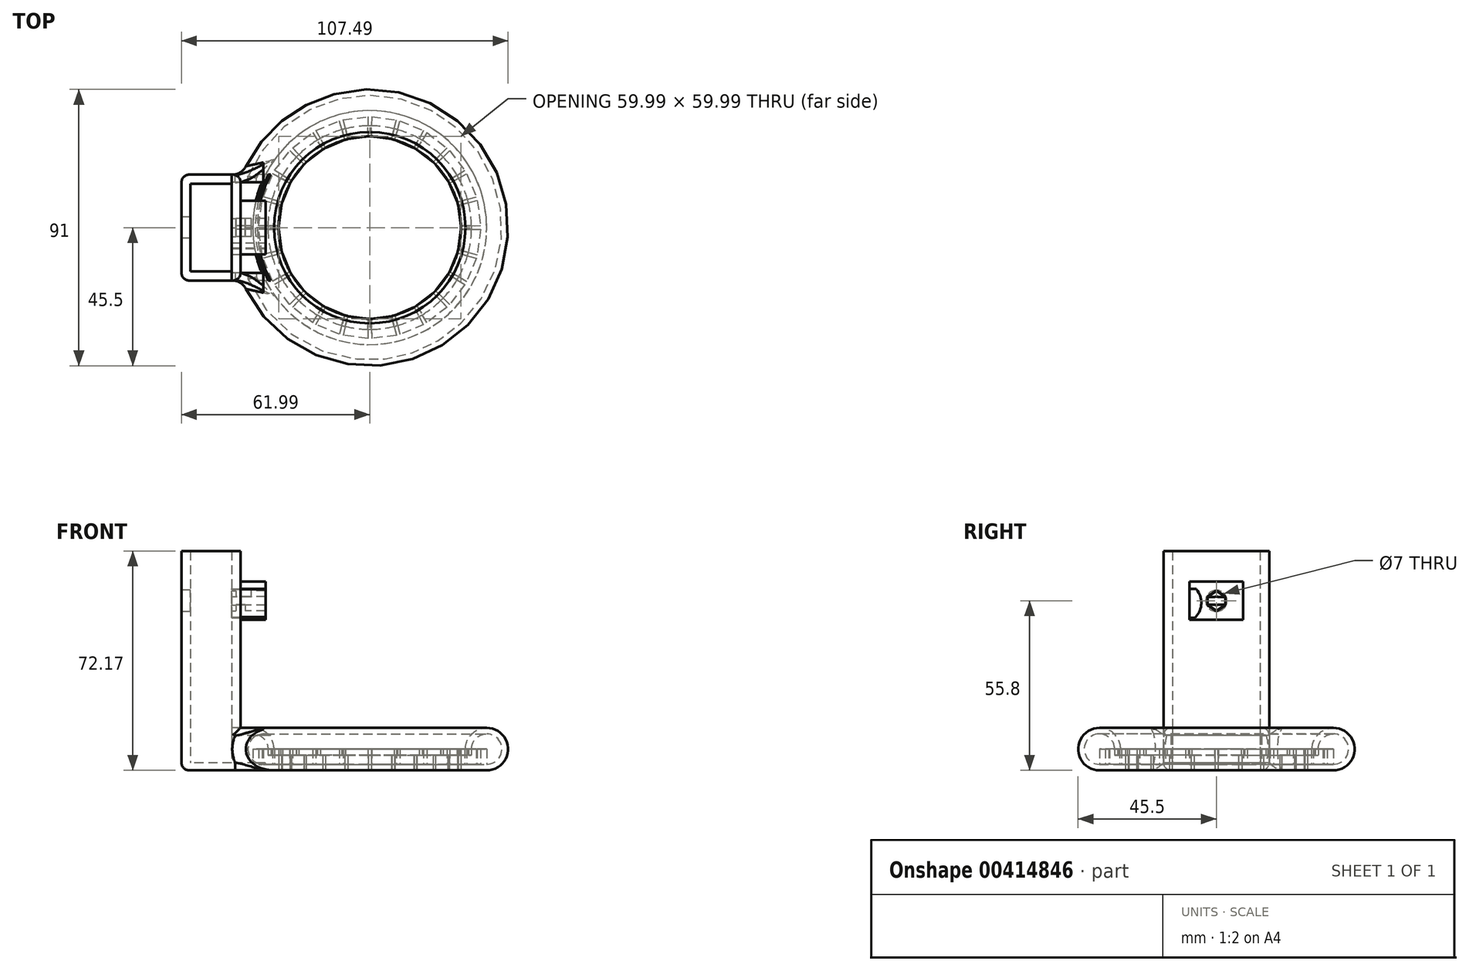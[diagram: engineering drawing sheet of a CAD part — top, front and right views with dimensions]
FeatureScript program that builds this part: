
annotation { "Feature Type Name" : "Feature", "Feature Type Description" : "" }
export const myFeature = defineFeature(function(context is Context, id is Id, definition is map)
    precondition{}
    {
        {
            var Q0;
            Q0=qCreatedBy(makeId("Right.planeOp"),FACE);
            cPlane(context, id + "F0", {"entities" : qUnion([Q0]), "cplaneType" : CPlaneType.OFFSET, "offset" : 42.5 * mm, "oppositeDirection" : true, "width" : 150 * mm, "height" : 150 * mm});
        }
        {
            var Q0;
            Q0=qCreatedBy(makeId("Front.planeOp"),FACE);
            cPlane(context, id + "F1", {"entities" : qUnion([Q0]), "cplaneType" : CPlaneType.OFFSET, "offset" : 17.41 * mm, "width" : 150 * mm, "height" : 150 * mm});
        }
        {
            var Q0;
            Q0=qCreatedBy(makeId("Front.planeOp"),FACE);
            cPlane(context, id + "F2", {"entities" : qUnion([Q0]), "cplaneType" : CPlaneType.OFFSET, "offset" : 17.41 * mm, "oppositeDirection" : true, "width" : 150 * mm, "height" : 150 * mm});
        }
        {
            var Q0;
            Q0=qCreatedBy(makeId("Top.planeOp"),FACE);
            cPlane(context, id + "F3", {"entities" : qUnion([Q0]), "cplaneType" : CPlaneType.OFFSET, "offset" : 7 * mm, "width" : 150 * mm, "height" : 150 * mm});
        }
        {
            var Q0;
            Q0=qCreatedBy(id+"F3.planeOp",FACE);
            cPlane(context, id + "F4", {"entities" : qUnion([Q0]), "cplaneType" : CPlaneType.OFFSET, "offset" : 6.95 * mm, "width" : 150 * mm, "height" : 150 * mm});
        }
        {
            var Q0;
            Q0=qCreatedBy(makeId("Right.planeOp"),FACE);
            cPlane(context, id + "F5", {"entities" : qUnion([Q0]), "cplaneType" : CPlaneType.OFFSET, "offset" : 62 * mm, "oppositeDirection" : true, "width" : 150 * mm, "height" : 150 * mm});
        }
        {
            var Q0;
            Q0=qCreatedBy(makeId("Top.planeOp"),FACE);
            var sketch = newSketch(context, id + "F6", { "sketchPlane" : qUnion([Q0])});
            skCircle(sketch, "E0", {"center": v(0, 0) * mm, "radius": 45 * mm});
            skCircle(sketch, "E1.0", {"center": v(0, 0) * mm, "radius": 38.5 * mm});
            skLineSegment(sketch, "E2", {"start": v(-136.41, 41.5) * mm, "end": v(-136.41, 35) * mm});
            skLineSegment(sketch, "E3", {"start": v(-128.72, 34) * mm, "end": v(-127.05, 40.28) * mm});
            skLineSegment(sketch, "E4", {"start": v(-118.16, 36.6) * mm, "end": v(-121.4, 30.99) * mm});
            skLineSegment(sketch, "E5", {"start": v(-115.15, 26.17) * mm, "end": v(-110.55, 30.76) * mm});
            skLineSegment(sketch, "E6", {"start": v(-110.44, 20.01) * mm, "end": v(-104.8, 23.26) * mm});
            skLineSegment(sketch, "E7", {"start": v(-107.45, 12.84) * mm, "end": v(-101.18, 14.54) * mm});
            skLineSegment(sketch, "E8", {"start": v(-106.41, 5.01) * mm, "end": v(-99.91, 5.01) * mm});
            skLineSegment(sketch, "E9.MirrorCS", {"start": v(-107.44, -2.81) * mm, "end": v(-101.17, -4.5) * mm});
            skLineSegment(sketch, "E10.MirrorCS", {"start": v(-110.42, -9.99) * mm, "end": v(-104.8, -13.24) * mm});
            skLineSegment(sketch, "E11.MirrorCS", {"start": v(-115.13, -16.15) * mm, "end": v(-110.52, -20.73) * mm});
            skLineSegment(sketch, "E12.MirrorCS", {"start": v(-118.13, -26.6) * mm, "end": v(-121.38, -20.97) * mm});
            skLineSegment(sketch, "E13.MirrorCS", {"start": v(-128.7, -24) * mm, "end": v(-127.02, -30.27) * mm});
            skLineSegment(sketch, "E14.MirrorCS", {"start": v(-144.1, 34) * mm, "end": v(-145.77, 40.28) * mm});
            skLineSegment(sketch, "E15.MirrorCS", {"start": v(-154.66, 36.6) * mm, "end": v(-151.41, 30.99) * mm});
            skLineSegment(sketch, "E16.MirrorCS", {"start": v(-157.67, 26.17) * mm, "end": v(-162.27, 30.76) * mm});
            skLineSegment(sketch, "E17.MirrorCS", {"start": v(-162.38, 20.01) * mm, "end": v(-168.01, 23.26) * mm});
            skLineSegment(sketch, "E18.MirrorCS", {"start": v(-165.37, 12.84) * mm, "end": v(-171.64, 14.54) * mm});
            skLineSegment(sketch, "E19.MirrorCS", {"start": v(-165.38, -2.81) * mm, "end": v(-171.65, -4.5) * mm});
            skLineSegment(sketch, "E20.MirrorCS", {"start": v(-162.4, -9.99) * mm, "end": v(-168.03, -13.24) * mm});
            skLineSegment(sketch, "E21.MirrorCS", {"start": v(-157.69, -16.15) * mm, "end": v(-162.3, -20.73) * mm});
            skLineSegment(sketch, "E22.MirrorCS", {"start": v(-154.69, -26.6) * mm, "end": v(-151.44, -20.97) * mm});
            skLineSegment(sketch, "E23.MirrorCS", {"start": v(-144.13, -24) * mm, "end": v(-145.8, -30.27) * mm});
            skLineSegment(sketch, "E24", {"start": v(-136.41, -25) * mm, "end": v(-136.41, -31.5) * mm});
            skLineSegment(sketch, "E25", {"start": v(-166.41, 5) * mm, "end": v(-172.91, 5) * mm});
            skCircle(sketch, "E26", {"center": v(-136.41, 5) * mm, "radius": 1.25 * mm, "construction": true});
            skLineSegment(sketch, "E27", {"start": v(0.64, 36.5) * mm, "end": v(0.52, 30) * mm});
            skLineSegment(sketch, "E28", {"start": v(8.2, 28.86) * mm, "end": v(9.97, 35.11) * mm});
            skLineSegment(sketch, "E29", {"start": v(18.8, 31.29) * mm, "end": v(15.46, 25.72) * mm});
            skLineSegment(sketch, "E30", {"start": v(21.62, 20.8) * mm, "end": v(26.3, 25.3) * mm});
            skLineSegment(sketch, "E31", {"start": v(26.23, 14.56) * mm, "end": v(31.92, 17.71) * mm});
            skLineSegment(sketch, "E32", {"start": v(29.1, 7.33) * mm, "end": v(35.4, 8.92) * mm});
            skLineSegment(sketch, "E33", {"start": v(30, -0.5) * mm, "end": v(36.5, -0.62) * mm});
            skLineSegment(sketch, "E34.MirrorCS", {"start": v(28.82, -8.32) * mm, "end": v(35.07, -10.12) * mm});
            skLineSegment(sketch, "E35.MirrorCS", {"start": v(25.72, -15.44) * mm, "end": v(31.3, -18.78) * mm});
            skLineSegment(sketch, "E36.MirrorCS", {"start": v(20.9, -21.52) * mm, "end": v(25.43, -26.18) * mm});
            skLineSegment(sketch, "E37.MirrorCS", {"start": v(17.73, -31.9) * mm, "end": v(14.57, -26.23) * mm});
            skLineSegment(sketch, "E38.MirrorCS", {"start": v(7.21, -29.12) * mm, "end": v(8.77, -35.43) * mm});
            skLineSegment(sketch, "E39.MirrorCS", {"start": v(-7.18, 29.13) * mm, "end": v(-8.74, 35.44) * mm});
            skLineSegment(sketch, "E40.MirrorCS", {"start": v(-17.7, 31.92) * mm, "end": v(-14.55, 26.25) * mm});
            skLineSegment(sketch, "E41.MirrorCS", {"start": v(-20.88, 21.54) * mm, "end": v(-25.4, 26.2) * mm});
            skLineSegment(sketch, "E42.MirrorCS", {"start": v(-25.7, 15.46) * mm, "end": v(-31.28, 18.81) * mm});
            skLineSegment(sketch, "E43.MirrorCS", {"start": v(-28.82, 8.34) * mm, "end": v(-35.06, 10.15) * mm});
            skLineSegment(sketch, "E44.MirrorCS", {"start": v(-29.1, -7.3) * mm, "end": v(-35.4, -8.89) * mm});
            skLineSegment(sketch, "E45.MirrorCS", {"start": v(-26.25, -14.53) * mm, "end": v(-31.93, -17.68) * mm});
            skLineSegment(sketch, "E46.MirrorCS", {"start": v(-21.64, -20.77) * mm, "end": v(-26.33, -25.28) * mm});
            skLineSegment(sketch, "E47.MirrorCS", {"start": v(-18.83, -31.27) * mm, "end": v(-15.48, -25.7) * mm});
            skLineSegment(sketch, "E48.MirrorCS", {"start": v(-8.22, -28.85) * mm, "end": v(-10, -35.1) * mm});
            skLineSegment(sketch, "E49", {"start": v(-0.52, -30) * mm, "end": v(-0.64, -36.5) * mm});
            skLineSegment(sketch, "E50", {"start": v(-30, 0.52) * mm, "end": v(-36.5, 0.64) * mm});
            skLineSegment(sketch, "E51", {"start": v(-0.64, 36.5) * mm, "end": v(-0.52, 30) * mm});
            skLineSegment(sketch, "E52", {"start": v(7.18, 29.13) * mm, "end": v(8.74, 35.44) * mm});
            skLineSegment(sketch, "E53", {"start": v(17.7, 31.92) * mm, "end": v(14.55, 26.25) * mm});
            skLineSegment(sketch, "E54", {"start": v(20.88, 21.54) * mm, "end": v(25.4, 26.2) * mm});
            skLineSegment(sketch, "E55", {"start": v(25.7, 15.46) * mm, "end": v(31.28, 18.81) * mm});
            skLineSegment(sketch, "E56", {"start": v(28.82, 8.34) * mm, "end": v(35.06, 10.15) * mm});
            skLineSegment(sketch, "E57", {"start": v(30, 0.54) * mm, "end": v(36.5, 0.65) * mm});
            skLineSegment(sketch, "E58.MirrorCS", {"start": v(29.1, -7.3) * mm, "end": v(35.4, -8.89) * mm});
            skLineSegment(sketch, "E59.MirrorCS", {"start": v(26.25, -14.53) * mm, "end": v(31.93, -17.68) * mm});
            skLineSegment(sketch, "E60.MirrorCS", {"start": v(21.64, -20.77) * mm, "end": v(26.33, -25.28) * mm});
            skLineSegment(sketch, "E61.MirrorCS", {"start": v(18.83, -31.27) * mm, "end": v(15.48, -25.7) * mm});
            skLineSegment(sketch, "E62.MirrorCS", {"start": v(8.22, -28.85) * mm, "end": v(10, -35.1) * mm});
            skLineSegment(sketch, "E63.MirrorCS", {"start": v(-8.2, 28.86) * mm, "end": v(-9.97, 35.11) * mm});
            skLineSegment(sketch, "E64.MirrorCS", {"start": v(-18.8, 31.29) * mm, "end": v(-15.46, 25.72) * mm});
            skLineSegment(sketch, "E65.MirrorCS", {"start": v(-21.62, 20.8) * mm, "end": v(-26.3, 25.3) * mm});
            skLineSegment(sketch, "E66.MirrorCS", {"start": v(-26.23, 14.56) * mm, "end": v(-31.92, 17.71) * mm});
            skLineSegment(sketch, "E67.MirrorCS", {"start": v(-29.1, 7.33) * mm, "end": v(-35.4, 8.92) * mm});
            skLineSegment(sketch, "E68.MirrorCS", {"start": v(-28.82, -8.32) * mm, "end": v(-35.07, -10.12) * mm});
            skLineSegment(sketch, "E69.MirrorCS", {"start": v(-25.72, -15.44) * mm, "end": v(-31.3, -18.78) * mm});
            skLineSegment(sketch, "E70.MirrorCS", {"start": v(-20.9, -21.52) * mm, "end": v(-25.43, -26.18) * mm});
            skLineSegment(sketch, "E71.MirrorCS", {"start": v(-17.73, -31.9) * mm, "end": v(-14.57, -26.23) * mm});
            skLineSegment(sketch, "E72.MirrorCS", {"start": v(-7.21, -29.12) * mm, "end": v(-8.77, -35.43) * mm});
            skLineSegment(sketch, "E73", {"start": v(0.52, -30) * mm, "end": v(0.64, -36.5) * mm});
            skLineSegment(sketch, "E74", {"start": v(-30, -0.52) * mm, "end": v(-36.5, -0.64) * mm});
            skCircle(sketch, "E75", {"center": v(0, 0) * mm, "radius": 1.25 * mm, "construction": true});
            skLineSegment(sketch, "E76", {"start": v(-29.1, 7.33) * mm, "end": v(-28.82, 8.34) * mm});
            skLineSegment(sketch, "E77", {"start": v(-28.82, 8.34) * mm, "end": v(-26.23, 14.56) * mm});
            skLineSegment(sketch, "E78", {"start": v(-26.23, 14.56) * mm, "end": v(-25.7, 15.46) * mm});
            skLineSegment(sketch, "E79", {"start": v(-25.7, 15.46) * mm, "end": v(-21.62, 20.8) * mm});
            skLineSegment(sketch, "E80", {"start": v(-21.62, 20.8) * mm, "end": v(-20.88, 21.54) * mm});
            skLineSegment(sketch, "E81", {"start": v(-20.88, 21.54) * mm, "end": v(-15.46, 25.72) * mm});
            skLineSegment(sketch, "E82", {"start": v(-15.46, 25.72) * mm, "end": v(-14.55, 26.25) * mm});
            skLineSegment(sketch, "E83", {"start": v(-14.55, 26.25) * mm, "end": v(-8.2, 28.86) * mm});
            skLineSegment(sketch, "E84", {"start": v(-8.2, 28.86) * mm, "end": v(-7.18, 29.13) * mm});
            skLineSegment(sketch, "E85", {"start": v(-7.18, 29.13) * mm, "end": v(-0.52, 30) * mm});
            skLineSegment(sketch, "E86", {"start": v(-0.52, 30) * mm, "end": v(0.52, 30) * mm});
            skLineSegment(sketch, "E87", {"start": v(0.52, 30) * mm, "end": v(7.18, 29.13) * mm});
            skLineSegment(sketch, "E88", {"start": v(7.18, 29.13) * mm, "end": v(8.2, 28.86) * mm});
            skLineSegment(sketch, "E89", {"start": v(8.2, 28.86) * mm, "end": v(14.55, 26.25) * mm});
            skLineSegment(sketch, "E90", {"start": v(14.55, 26.25) * mm, "end": v(15.46, 25.72) * mm});
            skLineSegment(sketch, "E91", {"start": v(15.46, 25.72) * mm, "end": v(20.88, 21.54) * mm});
            skLineSegment(sketch, "E92", {"start": v(20.88, 21.54) * mm, "end": v(21.62, 20.8) * mm});
            skLineSegment(sketch, "E93", {"start": v(21.62, 20.8) * mm, "end": v(25.7, 15.46) * mm});
            skLineSegment(sketch, "E94", {"start": v(25.7, 15.46) * mm, "end": v(26.23, 14.56) * mm});
            skLineSegment(sketch, "E95", {"start": v(26.23, 14.56) * mm, "end": v(28.82, 8.34) * mm});
            skLineSegment(sketch, "E96", {"start": v(28.82, 8.34) * mm, "end": v(29.1, 7.33) * mm});
            skLineSegment(sketch, "E97", {"start": v(29.1, 7.33) * mm, "end": v(30, 0.54) * mm});
            skLineSegment(sketch, "E98", {"start": v(30, 0.54) * mm, "end": v(30, -0.5) * mm});
            skLineSegment(sketch, "E99", {"start": v(30, -0.5) * mm, "end": v(29.1, -7.3) * mm});
            skLineSegment(sketch, "E100", {"start": v(29.1, -7.3) * mm, "end": v(28.82, -8.32) * mm});
            skLineSegment(sketch, "E101", {"start": v(28.82, -8.32) * mm, "end": v(26.25, -14.53) * mm});
            skLineSegment(sketch, "E102", {"start": v(26.25, -14.53) * mm, "end": v(25.72, -15.44) * mm});
            skLineSegment(sketch, "E103", {"start": v(25.72, -15.44) * mm, "end": v(21.64, -20.77) * mm});
            skLineSegment(sketch, "E104", {"start": v(21.64, -20.77) * mm, "end": v(20.9, -21.52) * mm});
            skLineSegment(sketch, "E105", {"start": v(20.9, -21.52) * mm, "end": v(15.48, -25.7) * mm});
            skLineSegment(sketch, "E106", {"start": v(15.48, -25.7) * mm, "end": v(14.57, -26.23) * mm});
            skLineSegment(sketch, "E107", {"start": v(14.57, -26.23) * mm, "end": v(8.22, -28.85) * mm});
            skLineSegment(sketch, "E108", {"start": v(8.22, -28.85) * mm, "end": v(7.21, -29.12) * mm});
            skLineSegment(sketch, "E109", {"start": v(7.21, -29.12) * mm, "end": v(0.52, -30) * mm});
            skLineSegment(sketch, "E110", {"start": v(0.52, -30) * mm, "end": v(-0.52, -30) * mm});
            skLineSegment(sketch, "E111", {"start": v(-0.52, -30) * mm, "end": v(-7.21, -29.12) * mm});
            skLineSegment(sketch, "E112", {"start": v(-7.21, -29.12) * mm, "end": v(-8.22, -28.85) * mm});
            skLineSegment(sketch, "E113", {"start": v(-8.22, -28.85) * mm, "end": v(-14.57, -26.23) * mm});
            skLineSegment(sketch, "E114", {"start": v(-14.57, -26.23) * mm, "end": v(-15.48, -25.7) * mm});
            skLineSegment(sketch, "E115", {"start": v(-15.48, -25.7) * mm, "end": v(-20.9, -21.52) * mm});
            skLineSegment(sketch, "E116", {"start": v(-20.9, -21.52) * mm, "end": v(-21.64, -20.77) * mm});
            skLineSegment(sketch, "E117", {"start": v(-21.64, -20.77) * mm, "end": v(-25.72, -15.44) * mm});
            skLineSegment(sketch, "E118", {"start": v(-25.72, -15.44) * mm, "end": v(-26.25, -14.53) * mm});
            skLineSegment(sketch, "E119", {"start": v(-28.82, -8.32) * mm, "end": v(-29.1, -7.3) * mm});
            skLineSegment(sketch, "E120", {"start": v(-26.25, -14.53) * mm, "end": v(-28.82, -8.32) * mm});
            skLineSegment(sketch, "E121", {"start": v(-29.1, -7.3) * mm, "end": v(-30, -0.52) * mm});
            skLineSegment(sketch, "E122", {"start": v(-30, -0.52) * mm, "end": v(-30, 0.52) * mm});
            skLineSegment(sketch, "E123", {"start": v(-30, 0.52) * mm, "end": v(-29.1, 7.33) * mm});
            skLineSegment(sketch, "E124", {"start": v(-36.5, 0.64) * mm, "end": v(-35.4, 8.92) * mm});
            skLineSegment(sketch, "E125", {"start": v(-35.06, 10.15) * mm, "end": v(-31.92, 17.71) * mm});
            skLineSegment(sketch, "E126", {"start": v(-31.28, 18.81) * mm, "end": v(-26.3, 25.3) * mm});
            skLineSegment(sketch, "E127", {"start": v(-25.4, 26.2) * mm, "end": v(-18.8, 31.29) * mm});
            skLineSegment(sketch, "E128", {"start": v(-17.7, 31.92) * mm, "end": v(-9.97, 35.11) * mm});
            skLineSegment(sketch, "E129", {"start": v(-8.74, 35.44) * mm, "end": v(-0.64, 36.5) * mm});
            skLineSegment(sketch, "E130", {"start": v(0.64, 36.5) * mm, "end": v(8.74, 35.44) * mm});
            skLineSegment(sketch, "E131", {"start": v(9.97, 35.11) * mm, "end": v(17.7, 31.92) * mm});
            skLineSegment(sketch, "E132", {"start": v(18.8, 31.29) * mm, "end": v(25.4, 26.2) * mm});
            skLineSegment(sketch, "E133", {"start": v(26.3, 25.3) * mm, "end": v(31.28, 18.81) * mm});
            skLineSegment(sketch, "E134", {"start": v(31.92, 17.71) * mm, "end": v(35.06, 10.15) * mm});
            skLineSegment(sketch, "E135", {"start": v(35.4, 8.92) * mm, "end": v(36.5, 0.65) * mm});
            skLineSegment(sketch, "E136", {"start": v(36.5, -0.62) * mm, "end": v(35.4, -8.89) * mm});
            skLineSegment(sketch, "E137", {"start": v(35.07, -10.12) * mm, "end": v(31.93, -17.68) * mm});
            skLineSegment(sketch, "E138", {"start": v(31.3, -18.78) * mm, "end": v(26.33, -25.28) * mm});
            skLineSegment(sketch, "E139", {"start": v(25.43, -26.18) * mm, "end": v(18.83, -31.27) * mm});
            skLineSegment(sketch, "E140", {"start": v(17.73, -31.9) * mm, "end": v(10, -35.1) * mm});
            skLineSegment(sketch, "E141", {"start": v(8.77, -35.43) * mm, "end": v(0.64, -36.5) * mm});
            skLineSegment(sketch, "E142", {"start": v(-0.64, -36.5) * mm, "end": v(-8.77, -35.43) * mm});
            skLineSegment(sketch, "E143", {"start": v(-10, -35.1) * mm, "end": v(-17.73, -31.9) * mm});
            skLineSegment(sketch, "E144", {"start": v(-18.83, -31.27) * mm, "end": v(-25.43, -26.18) * mm});
            skLineSegment(sketch, "E145", {"start": v(-26.33, -25.28) * mm, "end": v(-31.3, -18.78) * mm});
            skLineSegment(sketch, "E146", {"start": v(-31.93, -17.68) * mm, "end": v(-35.07, -10.12) * mm});
            skLineSegment(sketch, "E147", {"start": v(-35.4, -8.89) * mm, "end": v(-36.5, -0.64) * mm});
            skSolve(sketch);
        }
        {
            var Q0;
            Q0=qCreatedBy(makeId("Front.planeOp"),FACE);
            var sketch = newSketch(context, id + "F7", { "sketchPlane" : qUnion([Q0])});
            skLineSegment(sketch, "E148.bottom", {"start": v(38.5, 7) * mm, "end": v(-38.5, 7) * mm, "construction": true});
            skLineSegment(sketch, "E148.top", {"start": v(38.5, -7) * mm, "end": v(-38.5, -7) * mm, "construction": true});
            skLineSegment(sketch, "E148.left", {"start": v(38.5, 7) * mm, "end": v(38.5, -7) * mm, "construction": true});
            skLineSegment(sketch, "E148.right", {"start": v(-38.5, 7) * mm, "end": v(-38.5, -7) * mm, "construction": true});
            skPoint(sketch, "E148.middle", {"position": v(0, 0) * mm});
            skLineSegment(sketch, "E149", {"start": v(-38.5, 0) * mm, "end": v(38.5, 0) * mm, "construction": true});
            skArc(sketch, "E150", {"start": v(38.5, 0) * mm, "mid": v(43.45, 11.95) * mm, "end": v(31.5, 7) * mm});
            skArc(sketch, "E151", {"start": v(38.5, 2) * mm, "mid": v(42.04, 10.54) * mm, "end": v(33.5, 7) * mm});
            skLineSegment(sketch, "E152", {"start": v(38.5, 2) * mm, "end": v(38.5, 0) * mm});
            skLineSegment(sketch, "E153", {"start": v(38.5, 2) * mm, "end": v(31.5, 2) * mm, "construction": true});
            skLineSegment(sketch, "E154", {"start": v(31.5, 2) * mm, "end": v(31.5, 0) * mm, "construction": true});
            skLineSegment(sketch, "E155.0", {"start": v(38.5, 5) * mm, "end": v(-38.5, 5) * mm, "construction": true});
            skLineSegment(sketch, "E156", {"start": v(30, 0) * mm, "end": v(30, 7) * mm, "construction": true});
            skLineSegment(sketch, "E157", {"start": v(31.5, 7) * mm, "end": v(30, 7) * mm});
            skLineSegment(sketch, "E158", {"start": v(30, 7) * mm, "end": v(30, 5) * mm});
            skLineSegment(sketch, "E159", {"start": v(30, 5) * mm, "end": v(33.5, 5) * mm});
            skLineSegment(sketch, "E160", {"start": v(33.5, 5) * mm, "end": v(33.5, 7) * mm});
            skLineSegment(sketch, "E161", {"start": v(0, -7) * mm, "end": v(0, 7) * mm, "construction": true});
            skLineSegment(sketch, "E162", {"start": v(38.5, 7) * mm, "end": v(38.5, 14) * mm, "construction": true});
            skLineSegment(sketch, "E163", {"start": v(38.5, 7) * mm, "end": v(45.5, 7) * mm, "construction": true});
            skLineSegment(sketch, "E164", {"start": v(38.5, 12) * mm, "end": v(38.5, 14) * mm});
            skLineSegment(sketch, "E165", {"start": v(43.5, 7) * mm, "end": v(45.5, 7) * mm});
            skLineSegment(sketch, "E166.MirrorCS", {"start": v(-38.5, 2) * mm, "end": v(-38.5, 0) * mm});
            skLineSegment(sketch, "E167.MirrorCS", {"start": v(-30, 7) * mm, "end": v(-30, 5) * mm});
            skLineSegment(sketch, "E168.MirrorCS", {"start": v(-31.5, 7) * mm, "end": v(-30, 7) * mm});
            skLineSegment(sketch, "E169.MirrorCS", {"start": v(-33.5, 5) * mm, "end": v(-33.5, 7) * mm});
            skLineSegment(sketch, "E170.MirrorCS", {"start": v(-43.5, 7) * mm, "end": v(-45.5, 7) * mm});
            skLineSegment(sketch, "E171.MirrorCS", {"start": v(-30, 5) * mm, "end": v(-33.5, 5) * mm});
            skLineSegment(sketch, "E172.MirrorCS", {"start": v(-31.5, 2) * mm, "end": v(-31.5, 0) * mm, "construction": true});
            skLineSegment(sketch, "E173.MirrorCS", {"start": v(-38.5, 12) * mm, "end": v(-38.5, 14) * mm});
            skLineSegment(sketch, "E174.MirrorCS", {"start": v(-38.5, 7) * mm, "end": v(-45.5, 7) * mm, "construction": true});
            skLineSegment(sketch, "E175.MirrorCS", {"start": v(-38.5, 2) * mm, "end": v(-31.5, 2) * mm, "construction": true});
            skLineSegment(sketch, "E176.MirrorCS", {"start": v(-38.5, 7) * mm, "end": v(-38.5, 14) * mm, "construction": true});
            skArc(sketch, "E177.MirrorCS", {"start": v(-38.5, 0) * mm, "mid": v(-43.45, 11.95) * mm, "end": v(-31.5, 7) * mm});
            skArc(sketch, "E178.MirrorCS", {"start": v(-38.5, 2) * mm, "mid": v(-42.04, 10.54) * mm, "end": v(-33.5, 7) * mm});
            skLineSegment(sketch, "E179.MirrorCS", {"start": v(-38.5, 5) * mm, "end": v(38.5, 5) * mm, "construction": true});
            skLineSegment(sketch, "E180.MirrorCS", {"start": v(-30, 0) * mm, "end": v(-30, 7) * mm, "construction": true});
            skLineSegment(sketch, "E181.MirrorCS", {"start": v(-38.5, 7) * mm, "end": v(38.5, 7) * mm, "construction": true});
            skSolve(sketch);
        }
        {
            var Q0;
            Q0=qCreatedBy(id+"F0.planeOp",FACE);
            var sketch = newSketch(context, id + "F8", { "sketchPlane" : qUnion([Q0])});
            skLineSegment(sketch, "E182.bottom", {"start": v(45.5, 14) * mm, "end": v(-45.5, 14) * mm, "construction": true});
            skLineSegment(sketch, "E182.top", {"start": v(45.5, -14) * mm, "end": v(-45.5, -14) * mm, "construction": true});
            skLineSegment(sketch, "E182.left", {"start": v(45.5, 14) * mm, "end": v(45.5, -14) * mm, "construction": true});
            skLineSegment(sketch, "E182.right", {"start": v(-45.5, 14) * mm, "end": v(-45.5, -14) * mm, "construction": true});
            skPoint(sketch, "E182.middle", {"position": v(0, 0) * mm});
            skLineSegment(sketch, "E183", {"start": v(-45.5, 0) * mm, "end": v(45.5, 0) * mm, "construction": true});
            skLineSegment(sketch, "E184", {"start": v(0, 14) * mm, "end": v(0, -14) * mm, "construction": true});
            skLineSegment(sketch, "E185.0", {"start": v(-17.41, 14) * mm, "end": v(-17.41, -14) * mm, "construction": true});
            skLineSegment(sketch, "E186.MirrorCS", {"start": v(17.41, 14) * mm, "end": v(17.41, -14) * mm, "construction": true});
            skLineSegment(sketch, "E187.0", {"start": v(45.5, 7) * mm, "end": v(-45.5, 7) * mm, "construction": true});
            skLineSegment(sketch, "E188", {"start": v(-17.41, 14) * mm, "end": v(-17.41, 7) * mm});
            skLineSegment(sketch, "E189", {"start": v(-17.41, 7) * mm, "end": v(17.41, 7) * mm});
            skLineSegment(sketch, "E190", {"start": v(17.41, 7) * mm, "end": v(17.41, 14) * mm});
            skLineSegment(sketch, "E191", {"start": v(17.41, 14) * mm, "end": v(-17.41, 14) * mm});
            skLineSegment(sketch, "E192.0", {"start": v(45.5, 12) * mm, "end": v(-45.5, 12) * mm, "construction": true});
            skLineSegment(sketch, "E193.0", {"start": v(-14.73, 14) * mm, "end": v(-14.73, -14) * mm, "construction": true});
            skLineSegment(sketch, "E194.MirrorCS", {"start": v(14.73, 14) * mm, "end": v(14.73, -14) * mm, "construction": true});
            skLineSegment(sketch, "E195", {"start": v(-14.73, 7) * mm, "end": v(-14.73, 14) * mm});
            skLineSegment(sketch, "E196", {"start": v(14.73, 7) * mm, "end": v(14.73, 14) * mm});
            skLineSegment(sketch, "E197", {"start": v(17.41, 12) * mm, "end": v(-17.41, 12) * mm});
            skPoint(sketch, "E197.startSnap0", {"position": v(17.41, 10.5) * mm});
            skArc(sketch, "E198.0", {"start": v(6.63, 59.56) * mm, "mid": v(4.95, 54.97) * mm, "end": v(6.87, 50.47) * mm});
            skArc(sketch, "E199.MirrorCS", {"start": v(-6.63, 59.56) * mm, "mid": v(-4.95, 54.97) * mm, "end": v(-6.87, 50.47) * mm});
            skLineSegment(sketch, "E200", {"start": v(-6.63, 59.72) * mm, "end": v(6.63, 59.72) * mm});
            skLineSegment(sketch, "E201.1", {"start": v(-2.98, 51.95) * mm, "end": v(2.98, 51.95) * mm});
            skLineSegment(sketch, "E202", {"start": v(-8.8, 49.55) * mm, "end": v(-8.8, 62.12) * mm});
            skLineSegment(sketch, "E203.MirrorCS", {"start": v(8.8, 49.55) * mm, "end": v(8.8, 62.12) * mm});
            skLineSegment(sketch, "E204", {"start": v(-8.8, 62.12) * mm, "end": v(8.8, 62.12) * mm});
            skLineSegment(sketch, "E205", {"start": v(-6.63, 59.72) * mm, "end": v(-8.8, 59.72) * mm});
            skLineSegment(sketch, "E206", {"start": v(6.63, 59.72) * mm, "end": v(8.8, 59.72) * mm});
            skLineSegment(sketch, "E207", {"start": v(-2.98, 51.95) * mm, "end": v(-6.87, 50.26) * mm});
            skLineSegment(sketch, "E208", {"start": v(-6.87, 50.47) * mm, "end": v(-6.87, 50.26) * mm});
            skLineSegment(sketch, "E209.MirrorCS", {"start": v(2.98, 51.95) * mm, "end": v(6.87, 50.26) * mm});
            skLineSegment(sketch, "E210.MirrorCS", {"start": v(6.87, 50.47) * mm, "end": v(6.87, 50.26) * mm});
            skLineSegment(sketch, "E211", {"start": v(-8.8, 49.55) * mm, "end": v(8.8, 49.55) * mm});
            skLineSegment(sketch, "E212", {"start": v(6.87, 50.26) * mm, "end": v(8.8, 50.26) * mm});
            skLineSegment(sketch, "E213", {"start": v(-6.87, 50.26) * mm, "end": v(-8.8, 50.26) * mm});
            skCircle(sketch, "E214", {"center": v(0, 0) * mm, "radius": 1.5 * mm, "construction": true});
            skCircle(sketch, "E215", {"center": v(0, 55.8) * mm, "radius": 1.39 * mm});
            skLineSegment(sketch, "E216", {"start": v(6.63, 59.56) * mm, "end": v(6.63, 59.72) * mm});
            skLineSegment(sketch, "E217", {"start": v(-6.63, 59.56) * mm, "end": v(-6.63, 59.72) * mm});
            skLineSegment(sketch, "E218.1", {"start": v(0, 52.5) * mm, "end": v(2.95, 54.35) * mm});
            skLineSegment(sketch, "E218.2", {"start": v(-2.95, 54.35) * mm, "end": v(0, 52.5) * mm});
            skLineSegment(sketch, "E219.MirrorCS", {"start": v(0, 59.1) * mm, "end": v(2.95, 57.25) * mm});
            skLineSegment(sketch, "E220.MirrorCS", {"start": v(-2.95, 57.25) * mm, "end": v(0, 59.1) * mm});
            skLineSegment(sketch, "E221", {"start": v(2.95, 57.25) * mm, "end": v(2.95, 54.35) * mm});
            skLineSegment(sketch, "E222", {"start": v(-2.95, 57.25) * mm, "end": v(-2.95, 54.35) * mm});
            skCircle(sketch, "E223", {"center": v(0, 55.8) * mm, "radius": 1.25 * mm, "construction": true});
            skLineSegment(sketch, "E224", {"start": v(-2.95, 54.55) * mm, "end": v(2.95, 54.55) * mm});
            skLineSegment(sketch, "E225", {"start": v(-2.95, 57.05) * mm, "end": v(2.95, 57.05) * mm});
            skLineSegment(sketch, "E226", {"start": v(14.73, 14) * mm, "end": v(14.73, 52.5) * mm});
            skLineSegment(sketch, "E227", {"start": v(0, 55.8) * mm, "end": v(0, 14) * mm, "construction": true});
            skLineSegment(sketch, "E228.MirrorCS", {"start": v(-14.73, 14) * mm, "end": v(-14.73, 52.5) * mm});
            skLineSegment(sketch, "E229", {"start": v(17.41, 14) * mm, "end": v(17.41, 52.5) * mm});
            skLineSegment(sketch, "E230", {"start": v(-17.41, 14) * mm, "end": v(-17.41, 52.5) * mm});
            skLineSegment(sketch, "E231", {"start": v(17.41, 14) * mm, "end": v(17.41, 72.17) * mm});
            skLineSegment(sketch, "E232", {"start": v(17.41, 72.17) * mm, "end": v(-17.41, 72.17) * mm});
            skLineSegment(sketch, "E233", {"start": v(-17.41, 72.17) * mm, "end": v(-17.41, 52.5) * mm});
            skLineSegment(sketch, "E234", {"start": v(-14.73, 52.5) * mm, "end": v(-14.73, 72.17) * mm});
            skLineSegment(sketch, "E235", {"start": v(14.73, 52.5) * mm, "end": v(14.73, 72.17) * mm});
            skSolve(sketch);
        }
        {
            var Q0;
            Q0=qCreatedBy(id+"F1.planeOp",FACE);
            var sketch = newSketch(context, id + "F9", { "sketchPlane" : qUnion([Q0])});
            skLineSegment(sketch, "E236.bottom", {"start": v(45.5, 14) * mm, "end": v(-45.5, 14) * mm, "construction": true});
            skLineSegment(sketch, "E236.top", {"start": v(45.5, -14) * mm, "end": v(-45.5, -14) * mm, "construction": true});
            skLineSegment(sketch, "E236.left", {"start": v(45.5, 14) * mm, "end": v(45.5, -14) * mm, "construction": true});
            skLineSegment(sketch, "E236.right", {"start": v(-45.5, 14) * mm, "end": v(-45.5, -14) * mm, "construction": true});
            skPoint(sketch, "E236.middle", {"position": v(0, 0) * mm});
            skLineSegment(sketch, "E237", {"start": v(-45.5, 0) * mm, "end": v(45.5, 0) * mm, "construction": true});
            skLineSegment(sketch, "E238", {"start": v(0, 14) * mm, "end": v(0, -14) * mm, "construction": true});
            skLineSegment(sketch, "E239.0", {"start": v(-17.41, 14) * mm, "end": v(-17.41, -14) * mm, "construction": true});
            skLineSegment(sketch, "E240.MirrorCS", {"start": v(17.41, 14) * mm, "end": v(17.41, -14) * mm, "construction": true});
            skLineSegment(sketch, "E241.0", {"start": v(45.5, 7) * mm, "end": v(-45.5, 7) * mm, "construction": true});
            skLineSegment(sketch, "E242", {"start": v(-17.41, 14) * mm, "end": v(-17.41, 7) * mm});
            skLineSegment(sketch, "E243", {"start": v(-17.41, 7) * mm, "end": v(17.41, 7) * mm});
            skLineSegment(sketch, "E244", {"start": v(17.41, 7) * mm, "end": v(17.41, 14) * mm});
            skLineSegment(sketch, "E245", {"start": v(17.41, 14) * mm, "end": v(-17.41, 14) * mm});
            skLineSegment(sketch, "E246.0", {"start": v(45.5, 12) * mm, "end": v(-45.5, 12) * mm, "construction": true});
            skLineSegment(sketch, "E247.0", {"start": v(-14.73, 14) * mm, "end": v(-14.73, -14) * mm, "construction": true});
            skLineSegment(sketch, "E248.MirrorCS", {"start": v(14.73, 14) * mm, "end": v(14.73, -14) * mm, "construction": true});
            skLineSegment(sketch, "E249", {"start": v(-14.73, 7) * mm, "end": v(-14.73, 14) * mm});
            skLineSegment(sketch, "E250", {"start": v(14.73, 7) * mm, "end": v(14.73, 14) * mm});
            skLineSegment(sketch, "E251", {"start": v(17.41, 12) * mm, "end": v(-17.41, 12) * mm});
            skPoint(sketch, "E251.startSnap0", {"position": v(17.41, 10.5) * mm});
            skLineSegment(sketch, "E252", {"start": v(45.5, 14) * mm, "end": v(45.5, 7) * mm});
            skCircle(sketch, "E253", {"center": v(-35.07, 7) * mm, "radius": 7 * mm, "construction": true});
            skArc(sketch, "E254", {"start": v(-35.07, 12) * mm, "mid": v(-40.07, 7) * mm, "end": v(-35.07, 2) * mm});
            skLineSegment(sketch, "E255", {"start": v(-35.07, 12) * mm, "end": v(-35.07, 14) * mm});
            skLineSegment(sketch, "E256", {"start": v(-35.07, 14) * mm, "end": v(-45.5, 14) * mm});
            skLineSegment(sketch, "E257", {"start": v(-45.5, 14) * mm, "end": v(-45.5, 0) * mm});
            skLineSegment(sketch, "E258", {"start": v(-45.5, 0) * mm, "end": v(-35.07, 0) * mm});
            skLineSegment(sketch, "E259", {"start": v(-35.07, 0) * mm, "end": v(-35.07, 2) * mm});
            skLineSegment(sketch, "E260.MirrorCS", {"start": v(45.5, 2) * mm, "end": v(-45.5, 2) * mm, "construction": true});
            skCircle(sketch, "E261", {"center": v(0, 7) * mm, "radius": 1.25 * mm, "construction": true});
            skSolve(sketch);
        }
        {
            var Q0;
            Q0=qCreatedBy(id+"F2.planeOp",FACE);
            var sketch = newSketch(context, id + "F10", { "sketchPlane" : qUnion([Q0])});
            skLineSegment(sketch, "E262.bottom", {"start": v(45.5, 14) * mm, "end": v(-45.5, 14) * mm, "construction": true});
            skLineSegment(sketch, "E262.top", {"start": v(45.5, -14) * mm, "end": v(-45.5, -14) * mm, "construction": true});
            skLineSegment(sketch, "E262.left", {"start": v(45.5, 14) * mm, "end": v(45.5, -14) * mm, "construction": true});
            skLineSegment(sketch, "E262.right", {"start": v(-45.5, 14) * mm, "end": v(-45.5, -14) * mm, "construction": true});
            skPoint(sketch, "E262.middle", {"position": v(0, 0) * mm});
            skLineSegment(sketch, "E263", {"start": v(-45.5, 0) * mm, "end": v(45.5, 0) * mm, "construction": true});
            skLineSegment(sketch, "E264", {"start": v(0, 14) * mm, "end": v(0, -14) * mm, "construction": true});
            skLineSegment(sketch, "E265.0", {"start": v(-17.41, 14) * mm, "end": v(-17.41, -14) * mm, "construction": true});
            skLineSegment(sketch, "E266.MirrorCS", {"start": v(17.41, 14) * mm, "end": v(17.41, -14) * mm, "construction": true});
            skLineSegment(sketch, "E267.0", {"start": v(45.5, 7) * mm, "end": v(-45.5, 7) * mm, "construction": true});
            skLineSegment(sketch, "E268", {"start": v(-17.41, 14) * mm, "end": v(-17.41, 7) * mm});
            skLineSegment(sketch, "E269", {"start": v(-17.41, 7) * mm, "end": v(17.41, 7) * mm});
            skLineSegment(sketch, "E270", {"start": v(17.41, 7) * mm, "end": v(17.41, 14) * mm});
            skLineSegment(sketch, "E271", {"start": v(17.41, 14) * mm, "end": v(-17.41, 14) * mm});
            skLineSegment(sketch, "E272.0", {"start": v(45.5, 12) * mm, "end": v(-45.5, 12) * mm, "construction": true});
            skLineSegment(sketch, "E273.0", {"start": v(-14.73, 14) * mm, "end": v(-14.73, -14) * mm, "construction": true});
            skLineSegment(sketch, "E274.MirrorCS", {"start": v(14.73, 14) * mm, "end": v(14.73, -14) * mm, "construction": true});
            skLineSegment(sketch, "E275", {"start": v(-14.73, 7) * mm, "end": v(-14.73, 14) * mm});
            skLineSegment(sketch, "E276", {"start": v(14.73, 7) * mm, "end": v(14.73, 14) * mm});
            skLineSegment(sketch, "E277", {"start": v(17.41, 12) * mm, "end": v(-17.41, 12) * mm});
            skPoint(sketch, "E277.startSnap0", {"position": v(17.41, 10.5) * mm});
            skLineSegment(sketch, "E278", {"start": v(45.5, 14) * mm, "end": v(45.5, 7) * mm});
            skCircle(sketch, "E279", {"center": v(-35.07, 7) * mm, "radius": 7 * mm, "construction": true});
            skArc(sketch, "E280", {"start": v(-35.07, 12) * mm, "mid": v(-40.07, 7) * mm, "end": v(-35.07, 2) * mm});
            skLineSegment(sketch, "E281", {"start": v(-35.07, 12) * mm, "end": v(-35.07, 14) * mm});
            skLineSegment(sketch, "E282", {"start": v(-35.07, 14) * mm, "end": v(-45.5, 14) * mm});
            skLineSegment(sketch, "E283", {"start": v(-45.5, 14) * mm, "end": v(-45.5, 0) * mm});
            skLineSegment(sketch, "E284", {"start": v(-45.5, 0) * mm, "end": v(-35.07, 0) * mm});
            skLineSegment(sketch, "E285", {"start": v(-35.07, 0) * mm, "end": v(-35.07, 2) * mm});
            skLineSegment(sketch, "E286.MirrorCS", {"start": v(45.5, 2) * mm, "end": v(-45.5, 2) * mm, "construction": true});
            skCircle(sketch, "E287", {"center": v(0, 7) * mm, "radius": 1.25 * mm, "construction": true});
            skSolve(sketch);
        }
        {
            var Q0;
            Q0=qCreatedBy(makeId("Top.planeOp"),FACE);
            var sketch = newSketch(context, id + "F11", { "sketchPlane" : qUnion([Q0])});
            skPoint(sketch, "E288.middle", {"position": v(0, 0) * mm});
            skCircle(sketch, "E289", {"center": v(0, 0) * mm, "radius": 2.5 * mm, "construction": true});
            skLineSegment(sketch, "E290.MirrorCS", {"start": v(-32.65, 17.41) * mm, "end": v(-45.5, 17.41) * mm});
            skLineSegment(sketch, "E291.MirrorCS", {"start": v(-32.65, -17.41) * mm, "end": v(-45.5, -17.41) * mm});
            skLineSegment(sketch, "E292.MirrorCS", {"start": v(-45.5, 17.41) * mm, "end": v(-45.5, -17.41) * mm});
            skArc(sketch, "E293", {"start": v(-32.65, 17.41) * mm, "mid": v(-37, 0) * mm, "end": v(-32.65, -17.41) * mm});
            skLineSegment(sketch, "E294.bottom", {"start": v(-45.5, 8.28) * mm, "end": v(-45.5, -8.52) * mm, "construction": true});
            skLineSegment(sketch, "E294.left", {"start": v(-45.5, 8.28) * mm, "end": v(-59, 8.28) * mm, "construction": true});
            skLineSegment(sketch, "E295", {"start": v(-45.5, -8.52) * mm, "end": v(-59, -8.52) * mm, "construction": true});
            skLineSegment(sketch, "E296", {"start": v(-59, -8.52) * mm, "end": v(-59, 8.28) * mm, "construction": true});
            skLineSegment(sketch, "E297", {"start": v(-45.5, 8.28) * mm, "end": v(-59, -8.52) * mm, "construction": true});
            skLineSegment(sketch, "E298", {"start": v(-45.5, -8.52) * mm, "end": v(-59, 8.28) * mm, "construction": true});
            skLineSegment(sketch, "E299", {"start": v(-52.24, 0) * mm, "end": v(-42.5, 0) * mm, "construction": true});
            skLineSegment(sketch, "E300", {"start": v(-27.2, 0) * mm, "end": v(-42.4, 0) * mm, "construction": true});
            skLineSegment(sketch, "E301.0", {"start": v(-62, -8.52) * mm, "end": v(-62, 8.28) * mm, "construction": true});
            skLineSegment(sketch, "E302", {"start": v(-45.5, 17.41) * mm, "end": v(-62, 17.41) * mm});
            skLineSegment(sketch, "E303", {"start": v(-62, 17.41) * mm, "end": v(-62, -17.41) * mm});
            skLineSegment(sketch, "E304", {"start": v(-62, -17.41) * mm, "end": v(-45.5, -17.41) * mm});
            skLineSegment(sketch, "E305.0", {"start": v(-59, -14.41) * mm, "end": v(-45.5, -14.41) * mm});
            skLineSegment(sketch, "E305.1", {"start": v(-59, 14.41) * mm, "end": v(-59, -14.41) * mm});
            skLineSegment(sketch, "E305.2", {"start": v(-45.5, 14.41) * mm, "end": v(-59, 14.41) * mm});
            skSolve(sketch);
        }
        {
            var Q0;
            Q0=qCreatedBy(id+"F4.planeOp",FACE);
            var sketch = newSketch(context, id + "F12", { "sketchPlane" : qUnion([Q0])});
            skPoint(sketch, "E306.middle", {"position": v(0, 0) * mm});
            skCircle(sketch, "E307", {"center": v(0, 0) * mm, "radius": 2.5 * mm, "construction": true});
            skLineSegment(sketch, "E308.MirrorCS", {"start": v(-32.65, 17.41) * mm, "end": v(-45.5, 17.41) * mm});
            skLineSegment(sketch, "E309.MirrorCS", {"start": v(-32.65, -17.41) * mm, "end": v(-45.5, -17.41) * mm});
            skLineSegment(sketch, "E310.MirrorCS", {"start": v(-45.5, 17.41) * mm, "end": v(-45.5, -17.41) * mm});
            skArc(sketch, "E311", {"start": v(-32.65, 17.41) * mm, "mid": v(-37, 0) * mm, "end": v(-32.65, -17.41) * mm});
            skLineSegment(sketch, "E312.bottom", {"start": v(-45.5, 8.28) * mm, "end": v(-45.5, -8.52) * mm, "construction": true});
            skLineSegment(sketch, "E312.left", {"start": v(-45.5, 8.28) * mm, "end": v(-59, 8.28) * mm, "construction": true});
            skLineSegment(sketch, "E313", {"start": v(-45.5, -8.52) * mm, "end": v(-59, -8.52) * mm, "construction": true});
            skLineSegment(sketch, "E314", {"start": v(-59, -8.52) * mm, "end": v(-59, 8.28) * mm, "construction": true});
            skLineSegment(sketch, "E315", {"start": v(-45.5, 8.28) * mm, "end": v(-59, -8.52) * mm, "construction": true});
            skLineSegment(sketch, "E316", {"start": v(-45.5, -8.52) * mm, "end": v(-59, 8.28) * mm, "construction": true});
            skLineSegment(sketch, "E317", {"start": v(-52.24, 0) * mm, "end": v(-42.5, 0) * mm, "construction": true});
            skLineSegment(sketch, "E318", {"start": v(-27.2, 0) * mm, "end": v(-42.4, 0) * mm, "construction": true});
            skLineSegment(sketch, "E319.0", {"start": v(-62, -8.52) * mm, "end": v(-62, 8.28) * mm, "construction": true});
            skLineSegment(sketch, "E320", {"start": v(-45.5, 17.41) * mm, "end": v(-62, 17.41) * mm});
            skLineSegment(sketch, "E321", {"start": v(-62, 17.41) * mm, "end": v(-62, -17.41) * mm});
            skLineSegment(sketch, "E322", {"start": v(-62, -17.41) * mm, "end": v(-45.5, -17.41) * mm});
            skLineSegment(sketch, "E323.0", {"start": v(-59, -14.41) * mm, "end": v(-45.5, -14.41) * mm});
            skLineSegment(sketch, "E323.1", {"start": v(-59, 14.41) * mm, "end": v(-59, -14.41) * mm});
            skLineSegment(sketch, "E323.2", {"start": v(-45.5, 14.41) * mm, "end": v(-59, 14.41) * mm});
            skLineSegment(sketch, "E324.0", {"start": v(-42.5, 17.41) * mm, "end": v(-42.5, -17.41) * mm});
            skSolve(sketch);
        }
        {
            var Q0;
            Q0=makeQuery(id+"F6.imprint","IMPRINT",FACE,{"disambiguationData":[TD([[makeQuery(id+"F6.imprint","IMPRINT",EDGE,{"derivedFrom":sQuery(id+"F6.wireOp",EDGE,"E1.0")}),1.0]])]});
            extrude(context, id + "F13", {"entities" : qUnion([Q0]), "depth" : 7 * mm});
        }
        {
            var Q0;
            Q0=makeQuery(id+"F6.imprint","IMPRINT",FACE,{"disambiguationData":[TD([[makeQuery(id+"F6.imprint","IMPRINT",EDGE,{"derivedFrom":sQuery(id+"F6.wireOp",EDGE,"E50")}),-1.0]])]});
            var Q1;
            Q1=makeQuery(id+"F6.imprint","IMPRINT",FACE,{"disambiguationData":[TD([[makeQuery(id+"F6.imprint","IMPRINT",EDGE,{"derivedFrom":sQuery(id+"F6.wireOp",EDGE,"E43.MirrorCS")}),-1.0]])]});
            var Q2;
            Q2=makeQuery(id+"F6.imprint","IMPRINT",FACE,{"disambiguationData":[TD([[makeQuery(id+"F6.imprint","IMPRINT",EDGE,{"derivedFrom":sQuery(id+"F6.wireOp",EDGE,"E42.MirrorCS")}),-1.0]])]});
            var Q3;
            Q3=makeQuery(id+"F6.imprint","IMPRINT",FACE,{"disambiguationData":[TD([[makeQuery(id+"F6.imprint","IMPRINT",EDGE,{"derivedFrom":sQuery(id+"F6.wireOp",EDGE,"E41.MirrorCS")}),-1.0]])]});
            var Q4;
            Q4=makeQuery(id+"F6.imprint","IMPRINT",FACE,{"disambiguationData":[TD([[makeQuery(id+"F6.imprint","IMPRINT",EDGE,{"derivedFrom":sQuery(id+"F6.wireOp",EDGE,"E40.MirrorCS")}),1.0]])]});
            var Q5;
            Q5=makeQuery(id+"F6.imprint","IMPRINT",FACE,{"disambiguationData":[TD([[makeQuery(id+"F6.imprint","IMPRINT",EDGE,{"derivedFrom":sQuery(id+"F6.wireOp",EDGE,"E39.MirrorCS")}),-1.0]])]});
            var Q6;
            Q6=makeQuery(id+"F6.imprint","IMPRINT",FACE,{"disambiguationData":[TD([[makeQuery(id+"F6.imprint","IMPRINT",EDGE,{"derivedFrom":sQuery(id+"F6.wireOp",EDGE,"E27")}),1.0]])]});
            var Q7;
            Q7=makeQuery(id+"F6.imprint","IMPRINT",FACE,{"disambiguationData":[TD([[makeQuery(id+"F6.imprint","IMPRINT",EDGE,{"derivedFrom":sQuery(id+"F6.wireOp",EDGE,"E28")}),-1.0]])]});
            var Q8;
            Q8=makeQuery(id+"F6.imprint","IMPRINT",FACE,{"disambiguationData":[TD([[makeQuery(id+"F6.imprint","IMPRINT",EDGE,{"derivedFrom":sQuery(id+"F6.wireOp",EDGE,"E29")}),1.0]])]});
            var Q9;
            Q9=makeQuery(id+"F6.imprint","IMPRINT",FACE,{"disambiguationData":[TD([[makeQuery(id+"F6.imprint","IMPRINT",EDGE,{"derivedFrom":sQuery(id+"F6.wireOp",EDGE,"E30")}),-1.0]])]});
            var Q10;
            Q10=makeQuery(id+"F6.imprint","IMPRINT",FACE,{"disambiguationData":[TD([[makeQuery(id+"F6.imprint","IMPRINT",EDGE,{"derivedFrom":sQuery(id+"F6.wireOp",EDGE,"E31")}),-1.0]])]});
            var Q11;
            Q11=makeQuery(id+"F6.imprint","IMPRINT",FACE,{"disambiguationData":[TD([[makeQuery(id+"F6.imprint","IMPRINT",EDGE,{"derivedFrom":sQuery(id+"F6.wireOp",EDGE,"E32")}),-1.0]])]});
            var Q12;
            Q12=makeQuery(id+"F6.imprint","IMPRINT",FACE,{"disambiguationData":[TD([[makeQuery(id+"F6.imprint","IMPRINT",EDGE,{"derivedFrom":sQuery(id+"F6.wireOp",EDGE,"E33")}),-1.0]])]});
            var Q13;
            Q13=makeQuery(id+"F6.imprint","IMPRINT",FACE,{"disambiguationData":[TD([[makeQuery(id+"F6.imprint","IMPRINT",EDGE,{"derivedFrom":sQuery(id+"F6.wireOp",EDGE,"E34.MirrorCS")}),-1.0]])]});
            var Q14;
            Q14=makeQuery(id+"F6.imprint","IMPRINT",FACE,{"disambiguationData":[TD([[makeQuery(id+"F6.imprint","IMPRINT",EDGE,{"derivedFrom":sQuery(id+"F6.wireOp",EDGE,"E35.MirrorCS")}),-1.0]])]});
            var Q15;
            Q15=makeQuery(id+"F6.imprint","IMPRINT",FACE,{"disambiguationData":[TD([[makeQuery(id+"F6.imprint","IMPRINT",EDGE,{"derivedFrom":sQuery(id+"F6.wireOp",EDGE,"E36.MirrorCS")}),-1.0]])]});
            var Q16;
            Q16=makeQuery(id+"F6.imprint","IMPRINT",FACE,{"disambiguationData":[TD([[makeQuery(id+"F6.imprint","IMPRINT",EDGE,{"derivedFrom":sQuery(id+"F6.wireOp",EDGE,"E37.MirrorCS")}),1.0]])]});
            var Q17;
            Q17=makeQuery(id+"F6.imprint","IMPRINT",FACE,{"disambiguationData":[TD([[makeQuery(id+"F6.imprint","IMPRINT",EDGE,{"derivedFrom":sQuery(id+"F6.wireOp",EDGE,"E38.MirrorCS")}),-1.0]])]});
            var Q18;
            Q18=makeQuery(id+"F6.imprint","IMPRINT",FACE,{"disambiguationData":[TD([[makeQuery(id+"F6.imprint","IMPRINT",EDGE,{"derivedFrom":sQuery(id+"F6.wireOp",EDGE,"E49")}),-1.0]])]});
            var Q19;
            Q19=makeQuery(id+"F6.imprint","IMPRINT",FACE,{"disambiguationData":[TD([[makeQuery(id+"F6.imprint","IMPRINT",EDGE,{"derivedFrom":sQuery(id+"F6.wireOp",EDGE,"E48.MirrorCS")}),-1.0]])]});
            var Q20;
            Q20=makeQuery(id+"F6.imprint","IMPRINT",FACE,{"disambiguationData":[TD([[makeQuery(id+"F6.imprint","IMPRINT",EDGE,{"derivedFrom":sQuery(id+"F6.wireOp",EDGE,"E47.MirrorCS")}),1.0]])]});
            var Q21;
            Q21=makeQuery(id+"F6.imprint","IMPRINT",FACE,{"disambiguationData":[TD([[makeQuery(id+"F6.imprint","IMPRINT",EDGE,{"derivedFrom":sQuery(id+"F6.wireOp",EDGE,"E46.MirrorCS")}),-1.0]])]});
            var Q22;
            Q22=makeQuery(id+"F6.imprint","IMPRINT",FACE,{"disambiguationData":[TD([[makeQuery(id+"F6.imprint","IMPRINT",EDGE,{"derivedFrom":sQuery(id+"F6.wireOp",EDGE,"E45.MirrorCS")}),-1.0]])]});
            var Q23;
            Q23=makeQuery(id+"F6.imprint","IMPRINT",FACE,{"disambiguationData":[TD([[makeQuery(id+"F6.imprint","IMPRINT",EDGE,{"derivedFrom":sQuery(id+"F6.wireOp",EDGE,"E44.MirrorCS")}),-1.0]])]});
            extrude(context, id + "F14", {"entities" : qUnion([Q0, Q1, Q2, Q3, Q4, Q5, Q6, Q7, Q8, Q9, Q10, Q11, Q12, Q13, Q14, Q15, Q16, Q17, Q18, Q19, Q20, Q21, Q22, Q23]), "operationType" : NewBodyOperationType.ADD, "depth" : 2 * mm});
        }
        {
            var Q0;
            {var subQ0=sQuery(id+"F7.wireOp",EDGE,"E164");Q0=makeQuery(id+"F7.imprint","IMPRINT",FACE,{"disambiguationData":[TD([[makeQuery(id+"F7.imprint","IMPRINT",EDGE,{"derivedFrom":subQ0}),-1.0]])]});}
            var Q1;
            {var subQ0=sQuery(id+"F7.wireOp",EDGE,"E152");Q1=makeQuery(id+"F7.imprint","IMPRINT",FACE,{"disambiguationData":[TD([[makeQuery(id+"F7.imprint","IMPRINT",EDGE,{"derivedFrom":subQ0}),1.0]])]});}
            var Q2;
            Q2=sQuery(id+"F7.wireOp",EDGE,"E161");
            revolve(context, id + "F15", {"operationType" : NewBodyOperationType.ADD, "entities" : qUnion([Q0, Q1]), "axis" : qUnion([Q2]), "revolveType" : RevolveType.SYMMETRIC, "angle" : 315 * degree});
        }
        {
            var Q0;
            {var subQ3=sQuery(id+"F7.wireOp",EDGE,"E157");Q0=makeQuery(id+"F7.imprint","IMPRINT",FACE,{"disambiguationData":[TD([[makeQuery(id+"F7.imprint","IMPRINT",EDGE,{"derivedFrom":subQ3}),1.0]])]});}
            var Q1;
            Q1=sQuery(id+"F7.wireOp",EDGE,"E161");
            revolve(context, id + "F16", {"operationType" : NewBodyOperationType.ADD, "entities" : qUnion([Q0]), "axis" : qUnion([Q1]), "revolveType" : RevolveType.FULL});
        }
        {
            var Q0;
            Q0=makeQuery(id+"F10.imprint","IMPRINT",FACE,{"disambiguationData":[TD([[makeQuery(id+"F10.imprint","IMPRINT",EDGE,{"derivedFrom":sQuery(id+"F10.wireOp",EDGE,"E280")}),-1.0]])]});
            extrude(context, id + "F17", {"entities" : qUnion([Q0]), "operationType" : NewBodyOperationType.ADD, "depth" : 2.5 * mm});
        }
        {
            var Q0;
            Q0=makeQuery(id+"F9.imprint","IMPRINT",FACE,{"disambiguationData":[TD([[makeQuery(id+"F9.imprint","IMPRINT",EDGE,{"derivedFrom":sQuery(id+"F9.wireOp",EDGE,"E254")}),-1.0]])]});
            extrude(context, id + "F18", {"entities" : qUnion([Q0]), "operationType" : NewBodyOperationType.ADD, "oppositeDirection" : true, "depth" : 2.5 * mm});
        }
        {
            var Q0;
            Q0=makeQuery(id+"F11.imprint","IMPRINT",FACE,{"disambiguationData":[TD([[makeQuery(id+"F11.imprint","IMPRINT",EDGE,{"derivedFrom":sQuery(id+"F11.wireOp",EDGE,"E290.MirrorCS")}),1.0]])]});
            var Q1;
            {var subQ1=sQuery(id+"F11.wireOp",EDGE,"E294.bottom");Q1=makeQuery(id+"F11.imprint","IMPRINT",FACE,{"disambiguationData":[TD([[makeQuery(id+"F11.imprint","IMPRINT",EDGE,{"derivedFrom":subQ1}),1.0]])]});}
            var Q2;
            {var subQ5=sQuery(id+"F11.wireOp",EDGE,"E296");Q2=makeQuery(id+"F11.imprint","IMPRINT",FACE,{"disambiguationData":[TD([[makeQuery(id+"F11.imprint","IMPRINT",EDGE,{"derivedFrom":subQ5}),-1.0]])]});}
            var Q3;
            {var subQ0=sQuery(id+"F11.wireOp",EDGE,"E305.0");Q3=makeQuery(id+"F11.imprint","IMPRINT",FACE,{"disambiguationData":[TD([[makeQuery(id+"F11.imprint","IMPRINT",EDGE,{"derivedFrom":subQ0}),1.0]])]});}
            extrude(context, id + "F19", {"entities" : qUnion([Q0, Q1, Q2, Q3]), "operationType" : NewBodyOperationType.ADD, "depth" : 2.5 * mm});
        }
        {
            var Q0;
            {var subQ3=sQuery(id+"F12.wireOp",EDGE,"E308.MirrorCS");Q0=makeQuery(id+"F12.imprint","IMPRINT",FACE,{"disambiguationData":[TD([[makeQuery(id+"F12.imprint","IMPRINT",EDGE,{"derivedFrom":subQ3}),1.0]])]});}
            var Q1;
            {var subQ7=sQuery(id+"F12.wireOp",EDGE,"E324.0");Q1=makeQuery(id+"F12.imprint","IMPRINT",FACE,{"disambiguationData":[TD([[makeQuery(id+"F12.imprint","IMPRINT",EDGE,{"derivedFrom":subQ7}),-1.0]])]});}
            extrude(context, id + "F20", {"entities" : qUnion([Q0, Q1]), "operationType" : NewBodyOperationType.ADD, "oppositeDirection" : true, "depth" : 2.5 * mm});
        }
        {
            var Q0;
            {var subQ4=sQuery(id+"F11.wireOp",EDGE,"E296");Q0=makeQuery(id+"F11.imprint","IMPRINT",FACE,{"disambiguationData":[TD([[makeQuery(id+"F11.imprint","IMPRINT",EDGE,{"derivedFrom":subQ4}),1.0]])]});}
            var Q1;
            {var subQ0=sQuery(id+"F11.wireOp",EDGE,"6jEM1cKR-Vwea-ILg7-sG8q-rrc46WkZxeoR");Q1=makeQuery(id+"F11.imprint","IMPRINT",FACE,{"disambiguationData":[TD([[makeQuery(id+"F11.imprint","IMPRINT",EDGE,{"derivedFrom":subQ0}),-1.0]])]});}
            var Q2;
            {var subQ0=sQuery(id+"F11.wireOp",EDGE,"E302");Q2=makeQuery(id+"F11.imprint","IMPRINT",FACE,{"disambiguationData":[TD([[makeQuery(id+"F11.imprint","IMPRINT",EDGE,{"derivedFrom":subQ0}),1.0]])]});}
            extrude(context, id + "F21", {"entities" : qUnion([Q0, Q1, Q2]), "operationType" : NewBodyOperationType.ADD, "depth" : 14 * mm});
        }
        {
            var Q0;
            {var subQ0=sQuery(id+"F12.wireOp",EDGE,"E320");Q0=makeQuery(id+"F12.imprint","IMPRINT",FACE,{"disambiguationData":[TD([[makeQuery(id+"F12.imprint","IMPRINT",EDGE,{"derivedFrom":subQ0}),1.0]])]});}
            extrude(context, id + "F22", {"entities" : qUnion([Q0]), "operationType" : NewBodyOperationType.ADD, "depth" : 58.17 * mm});
        }
        {
            var Q0;
            Q0=makeQuery(id+"F8.imprint","IMPRINT",FACE,{"disambiguationData":[TD([[makeQuery(id+"F8.imprint","IMPRINT",EDGE,{"derivedFrom":sQuery(id+"F8.wireOp",EDGE,"E200")}),-1.0]])]});
            var Q1;
            {var subQ0=sQuery(id+"F8.wireOp",EDGE,"6a0bf37f-b3f9-4be4-bbcd-48762ca18b15");Q1=makeQuery(id+"F8.imprint","IMPRINT",FACE,{"disambiguationData":[TD([[makeQuery(id+"F8.imprint","IMPRINT",EDGE,{"derivedFrom":subQ0}),-1.0]])]});}
            var Q2;
            Q2=makeQuery(id+"F8.imprint","IMPRINT",FACE,{"disambiguationData":[TD([[makeQuery(id+"F8.imprint","IMPRINT",EDGE,{"derivedFrom":sQuery(id+"F8.wireOp",EDGE,"E200")}),1.0]])]});
            var Q3;
            Q3=makeQuery(id+"F8.imprint","IMPRINT",FACE,{"disambiguationData":[TD([[makeQuery(id+"F8.imprint","IMPRINT",EDGE,{"derivedFrom":sQuery(id+"F8.wireOp",EDGE,"E201.1")}),-1.0]])]});
            var Q4;
            {var subQ0=sQuery(id+"F8.wireOp",EDGE,"36538cae-b972-4159-a8ab-ed7d0897e562");Q4=makeQuery(id+"F8.imprint","IMPRINT",FACE,{"disambiguationData":[TD([[makeQuery(id+"F8.imprint","IMPRINT",EDGE,{"derivedFrom":subQ0}),1.0]])]});}
            var Q5;
            Q5=makeQuery(id+"F8.imprint","IMPRINT",FACE,{"disambiguationData":[TD([[makeQuery(id+"F8.imprint","IMPRINT",EDGE,{"derivedFrom":sQuery(id+"F8.wireOp",EDGE,"E199.MirrorCS")}),-1.0]])]});
            var Q6;
            Q6=makeQuery(id+"F8.imprint","IMPRINT",FACE,{"disambiguationData":[TD([[makeQuery(id+"F8.imprint","IMPRINT",EDGE,{"derivedFrom":sQuery(id+"F8.wireOp",EDGE,"E198.0")}),1.0]])]});
            var Q7;
            {var subQ2=sQuery(id+"F8.wireOp",EDGE,"E228.MirrorCS");Q7=makeQuery(id+"F8.imprint","IMPRINT",FACE,{"disambiguationData":[TD([[makeQuery(id+"F8.imprint","IMPRINT",EDGE,{"derivedFrom":subQ2}),1.0]])]});}
            var Q8;
            {var subQ0=sQuery(id+"F8.wireOp",EDGE,"E211");Q8=makeQuery(id+"F8.imprint","IMPRINT",FACE,{"disambiguationData":[TD([[makeQuery(id+"F8.imprint","IMPRINT",EDGE,{"derivedFrom":subQ0}),-1.0]])]});}
            var Q9;
            {var subQ2=sQuery(id+"F8.wireOp",EDGE,"E226");Q9=makeQuery(id+"F8.imprint","IMPRINT",FACE,{"disambiguationData":[TD([[makeQuery(id+"F8.imprint","IMPRINT",EDGE,{"derivedFrom":subQ2}),-1.0]])]});}
            extrude(context, id + "F23", {"entities" : qUnion([Q0, Q1, Q2, Q3, Q4, Q5, Q6, Q7, Q8, Q9]), "operationType" : NewBodyOperationType.ADD, "oppositeDirection" : true, "depth" : 3 * mm});
        }
        {
            var Q0;
            {var subQ1=sQuery(id+"F8.wireOp",EDGE,"E219.MirrorCS");Q0=makeQuery(id+"F8.imprint","IMPRINT",FACE,{"disambiguationData":[TD([[makeQuery(id+"F8.imprint","IMPRINT",EDGE,{"derivedFrom":subQ1}),-1.0]])]});}
            var Q1;
            {var subQ0=sQuery(id+"F8.wireOp",EDGE,"E225");var subQ1=sQuery(id+"F8.wireOp",EDGE,"E215");var subQ2=makeQuery(id+"F8.imprint","INTERSECT",VERTEX,{"disambiguationData":[OD(0.0)],"derivedFrom":[subQ1,subQ0]});Q1=makeQuery(id+"F8.imprint","IMPRINT",FACE,{"disambiguationData":[TD([[makeQuery(id+"F8.imprint","IMPRINT",EDGE,{"disambiguationData":[TD([[subQ2,-1.0]])],"derivedFrom":subQ1}),-1.0]])]});}
            var Q2;
            {var subQ0=sQuery(id+"F8.wireOp",EDGE,"E225");var subQ1=sQuery(id+"F8.wireOp",EDGE,"E215");var subQ2=makeQuery(id+"F8.imprint","INTERSECT",VERTEX,{"disambiguationData":[OD(1.0)],"derivedFrom":[subQ1,subQ0]});Q2=makeQuery(id+"F8.imprint","IMPRINT",FACE,{"disambiguationData":[TD([[makeQuery(id+"F8.imprint","IMPRINT",EDGE,{"disambiguationData":[TD([[subQ2,1.0]])],"derivedFrom":subQ1}),-1.0]])]});}
            var Q3;
            {var subQ0=sQuery(id+"F8.wireOp",EDGE,"E218.1");Q3=makeQuery(id+"F8.imprint","IMPRINT",FACE,{"disambiguationData":[TD([[makeQuery(id+"F8.imprint","IMPRINT",EDGE,{"derivedFrom":subQ0}),1.0]])]});}
            var Q4;
            Q4=makeQuery(id+"F8.imprint","IMPRINT",FACE,{"disambiguationData":[TD([[makeQuery(id+"F8.imprint","IMPRINT",EDGE,{"derivedFrom":sQuery(id+"F8.wireOp",EDGE,"E198.0")}),-1.0]])]});
            extrude(context, id + "F24", {"entities" : qUnion([Q0, Q1, Q2, Q3, Q4]), "operationType" : NewBodyOperationType.ADD, "endBound" : BoundingType.SYMMETRIC, "depth" : 3 * mm});
        }
        {
            var Q0;
            {var subQ0=sQuery(id+"F8.wireOp",EDGE,"E225");var subQ1=sQuery(id+"F8.wireOp",EDGE,"E215");var subQ2=makeQuery(id+"F8.imprint","INTERSECT",VERTEX,{"disambiguationData":[OD(1.0)],"derivedFrom":[subQ1,subQ0]});Q0=makeQuery(id+"F8.imprint","IMPRINT",FACE,{"disambiguationData":[TD([[makeQuery(id+"F8.imprint","IMPRINT",EDGE,{"disambiguationData":[TD([[subQ2,1.0]])],"derivedFrom":subQ1}),-1.0]])]});}
            var Q1;
            {var subQ0=sQuery(id+"F8.wireOp",EDGE,"E225");var subQ1=sQuery(id+"F8.wireOp",EDGE,"E215");var subQ2=makeQuery(id+"F8.imprint","INTERSECT",VERTEX,{"disambiguationData":[OD(0.0)],"derivedFrom":[subQ1,subQ0]});Q1=makeQuery(id+"F8.imprint","IMPRINT",FACE,{"disambiguationData":[TD([[makeQuery(id+"F8.imprint","IMPRINT",EDGE,{"disambiguationData":[TD([[subQ2,-1.0]])],"derivedFrom":subQ1}),-1.0]])]});}
            extrude(context, id + "F25", {"entities" : qUnion([Q0, Q1]), "operationType" : NewBodyOperationType.ADD, "depth" : 3.5 * mm});
        }
        {
            var Q0;
            Q0=makeQuery(id+"F8.imprint","IMPRINT",FACE,{"disambiguationData":[TD([[makeQuery(id+"F8.imprint","IMPRINT",EDGE,{"derivedFrom":sQuery(id+"F8.wireOp",EDGE,"E199.MirrorCS")}),-1.0]])]});
            var Q1;
            Q1=makeQuery(id+"F8.imprint","IMPRINT",FACE,{"disambiguationData":[TD([[makeQuery(id+"F8.imprint","IMPRINT",EDGE,{"derivedFrom":sQuery(id+"F8.wireOp",EDGE,"E200")}),1.0]])]});
            var Q2;
            Q2=makeQuery(id+"F8.imprint","IMPRINT",FACE,{"disambiguationData":[TD([[makeQuery(id+"F8.imprint","IMPRINT",EDGE,{"derivedFrom":sQuery(id+"F8.wireOp",EDGE,"E198.0")}),1.0]])]});
            var Q3;
            Q3=makeQuery(id+"F8.imprint","IMPRINT",FACE,{"disambiguationData":[TD([[makeQuery(id+"F8.imprint","IMPRINT",EDGE,{"derivedFrom":sQuery(id+"F8.wireOp",EDGE,"E201.1")}),-1.0]])]});
            extrude(context, id + "F26", {"entities" : qUnion([Q0, Q1, Q2, Q3]), "operationType" : NewBodyOperationType.ADD, "depth" : 8.2 * mm});
        }
        {
            var Q0;
            {var subQ0=sQuery(id+"F6.wireOp",EDGE,"E145");var subQ1=sQuery(id+"F6.wireOp",EDGE,"E69.MirrorCS");var subQ2=sQuery(id+"F6.wireOp",EDGE,"E46.MirrorCS");var subQ3=makeQuery(id+"F14.opExtrude","CAP_FACE",FACE,{"disambiguationData":[OSD([subQ2,subQ1,sQuery(id+"F6.wireOp",EDGE,"E117"),subQ0])],"isStart":true});var subQ4=sQuery(id+"F10.wireOp",EDGE,"E285");var subQ5=sQuery(id+"F10.wireOp",EDGE,"E284");var subQ6=sQuery(id+"F10.wireOp",EDGE,"E283");var subQ7=sQuery(id+"F10.wireOp",EDGE,"E282");var subQ8=sQuery(id+"F10.wireOp",EDGE,"E281");var subQ9=sQuery(id+"F10.wireOp",EDGE,"E280");var subQ10=makeQuery(id+"F17.opExtrude","CAP_FACE",FACE,{"disambiguationData":[OSD([subQ9,subQ8,subQ7,subQ6,subQ5,subQ4])],"isStart":false});var subQ11=sQuery(id+"F6.wireOp",EDGE,"E146");var subQ12=sQuery(id+"F6.wireOp",EDGE,"E68.MirrorCS");var subQ13=sQuery(id+"F6.wireOp",EDGE,"E45.MirrorCS");var subQ14=makeQuery(id+"F14.opExtrude","CAP_FACE",FACE,{"disambiguationData":[OSD([subQ13,subQ12,sQuery(id+"F6.wireOp",EDGE,"E120"),subQ11])],"isStart":true});var subQ15=makeQuery(id+"F16.opRevolve","SWEPT_FACE",FACE,{"disambiguationData":[OSD([sQuery(id+"F7.wireOp",EDGE,"E157")])]});var subQ16=sQuery(id+"F6.wireOp",EDGE,"E147");var subQ17=sQuery(id+"F6.wireOp",EDGE,"E74");var subQ18=sQuery(id+"F6.wireOp",EDGE,"E44.MirrorCS");var subQ19=makeQuery(id+"F14.opExtrude","CAP_FACE",FACE,{"disambiguationData":[OSD([subQ18,subQ17,sQuery(id+"F6.wireOp",EDGE,"E121"),subQ16])],"isStart":true});var subQ20=sQuery(id+"F7.wireOp",EDGE,"E164");var subQ21=sQuery(id+"F7.wireOp",EDGE,"E152");var subQ22=sQuery(id+"F7.wireOp",EDGE,"E151");var subQ23=sQuery(id+"F7.wireOp",EDGE,"E150");var subQ24=makeQuery(id+"F15.opRevolve","CAP_FACE",FACE,{"disambiguationData":[OSD([subQ23,subQ22,subQ21,subQ20])],"isStart":false});var subQ25=sQuery(id+"F6.wireOp",EDGE,"E125");var subQ26=sQuery(id+"F6.wireOp",EDGE,"E66.MirrorCS");var subQ27=sQuery(id+"F6.wireOp",EDGE,"E43.MirrorCS");var subQ28=makeQuery(id+"F14.opExtrude","CAP_FACE",FACE,{"disambiguationData":[OSD([subQ27,subQ26,sQuery(id+"F6.wireOp",EDGE,"E77"),subQ25])],"isStart":true});var subQ29=sQuery(id+"F6.wireOp",EDGE,"E126");var subQ30=sQuery(id+"F6.wireOp",EDGE,"E65.MirrorCS");var subQ31=sQuery(id+"F6.wireOp",EDGE,"E42.MirrorCS");var subQ32=makeQuery(id+"F14.opExtrude","CAP_FACE",FACE,{"disambiguationData":[OSD([subQ31,subQ30,sQuery(id+"F6.wireOp",EDGE,"E79"),subQ29])],"isStart":true});var subQ33=sQuery(id+"F6.wireOp",EDGE,"E127");var subQ34=sQuery(id+"F6.wireOp",EDGE,"E64.MirrorCS");var subQ35=sQuery(id+"F6.wireOp",EDGE,"E41.MirrorCS");var subQ36=makeQuery(id+"F14.opExtrude","CAP_FACE",FACE,{"disambiguationData":[OSD([subQ35,subQ34,sQuery(id+"F6.wireOp",EDGE,"E81"),subQ33])],"isStart":true});var subQ37=sQuery(id+"F6.wireOp",EDGE,"E128");var subQ38=sQuery(id+"F6.wireOp",EDGE,"E63.MirrorCS");var subQ39=sQuery(id+"F6.wireOp",EDGE,"E40.MirrorCS");var subQ40=makeQuery(id+"F14.opExtrude","CAP_FACE",FACE,{"disambiguationData":[OSD([subQ39,subQ38,sQuery(id+"F6.wireOp",EDGE,"E83"),subQ37])],"isStart":true});var subQ41=sQuery(id+"F6.wireOp",EDGE,"E129");var subQ42=sQuery(id+"F6.wireOp",EDGE,"E51");var subQ43=sQuery(id+"F6.wireOp",EDGE,"E39.MirrorCS");var subQ44=makeQuery(id+"F14.opExtrude","CAP_FACE",FACE,{"disambiguationData":[OSD([subQ43,subQ42,sQuery(id+"F6.wireOp",EDGE,"E85"),subQ41])],"isStart":true});var subQ45=sQuery(id+"F6.wireOp",EDGE,"E141");var subQ46=sQuery(id+"F6.wireOp",EDGE,"E73");var subQ47=sQuery(id+"F6.wireOp",EDGE,"E38.MirrorCS");var subQ48=makeQuery(id+"F14.opExtrude","CAP_FACE",FACE,{"disambiguationData":[OSD([subQ47,subQ46,sQuery(id+"F6.wireOp",EDGE,"E109"),subQ45])],"isStart":true});var subQ49=sQuery(id+"F6.wireOp",EDGE,"E140");var subQ50=sQuery(id+"F6.wireOp",EDGE,"E62.MirrorCS");var subQ51=sQuery(id+"F6.wireOp",EDGE,"E37.MirrorCS");var subQ52=makeQuery(id+"F14.opExtrude","CAP_FACE",FACE,{"disambiguationData":[OSD([subQ51,subQ50,sQuery(id+"F6.wireOp",EDGE,"E107"),subQ49])],"isStart":true});var subQ53=sQuery(id+"F6.wireOp",EDGE,"E139");var subQ54=sQuery(id+"F6.wireOp",EDGE,"E61.MirrorCS");var subQ55=sQuery(id+"F6.wireOp",EDGE,"E36.MirrorCS");var subQ56=makeQuery(id+"F14.opExtrude","CAP_FACE",FACE,{"disambiguationData":[OSD([subQ55,subQ54,sQuery(id+"F6.wireOp",EDGE,"E105"),subQ53])],"isStart":true});var subQ57=sQuery(id+"F6.wireOp",EDGE,"E138");var subQ58=sQuery(id+"F6.wireOp",EDGE,"E60.MirrorCS");var subQ59=sQuery(id+"F6.wireOp",EDGE,"E35.MirrorCS");var subQ60=makeQuery(id+"F14.opExtrude","CAP_FACE",FACE,{"disambiguationData":[OSD([subQ59,subQ58,sQuery(id+"F6.wireOp",EDGE,"E103"),subQ57])],"isStart":true});var subQ61=sQuery(id+"F6.wireOp",EDGE,"E131");var subQ62=sQuery(id+"F6.wireOp",EDGE,"E53");var subQ63=sQuery(id+"F6.wireOp",EDGE,"E28");var subQ64=makeQuery(id+"F14.opExtrude","CAP_FACE",FACE,{"disambiguationData":[OSD([subQ63,subQ62,sQuery(id+"F6.wireOp",EDGE,"E89"),subQ61])],"isStart":true});var subQ65=makeQuery(id+"F15.opRevolve","CAP_FACE",FACE,{"disambiguationData":[OSD([subQ23,subQ22,subQ21,subQ20])],"isStart":true});var subQ66=sQuery(id+"F6.wireOp",EDGE,"E130");var subQ67=sQuery(id+"F6.wireOp",EDGE,"E52");var subQ68=sQuery(id+"F6.wireOp",EDGE,"E27");var subQ69=makeQuery(id+"F14.opExtrude","CAP_FACE",FACE,{"disambiguationData":[OSD([subQ68,subQ67,sQuery(id+"F6.wireOp",EDGE,"E87"),subQ66])],"isStart":true});var subQ70=sQuery(id+"F6.wireOp",EDGE,"E144");var subQ71=sQuery(id+"F6.wireOp",EDGE,"E143");var subQ72=sQuery(id+"F6.wireOp",EDGE,"E142");var subQ73=sQuery(id+"F6.wireOp",EDGE,"E137");var subQ74=sQuery(id+"F6.wireOp",EDGE,"E136");var subQ75=sQuery(id+"F6.wireOp",EDGE,"E135");var subQ76=sQuery(id+"F6.wireOp",EDGE,"E134");var subQ77=sQuery(id+"F6.wireOp",EDGE,"E133");var subQ78=sQuery(id+"F6.wireOp",EDGE,"E132");var subQ79=sQuery(id+"F6.wireOp",EDGE,"E124");var subQ80=sQuery(id+"F6.wireOp",EDGE,"E122");var subQ81=sQuery(id+"F6.wireOp",EDGE,"E119");var subQ82=sQuery(id+"F6.wireOp",EDGE,"E118");var subQ83=sQuery(id+"F6.wireOp",EDGE,"E116");var subQ84=sQuery(id+"F6.wireOp",EDGE,"E114");var subQ85=sQuery(id+"F6.wireOp",EDGE,"E112");var subQ86=sQuery(id+"F6.wireOp",EDGE,"E110");var subQ87=sQuery(id+"F6.wireOp",EDGE,"E108");var subQ88=sQuery(id+"F6.wireOp",EDGE,"E106");var subQ89=sQuery(id+"F6.wireOp",EDGE,"E104");var subQ90=sQuery(id+"F6.wireOp",EDGE,"E102");var subQ91=sQuery(id+"F6.wireOp",EDGE,"E100");var subQ92=sQuery(id+"F6.wireOp",EDGE,"E98");var subQ93=sQuery(id+"F6.wireOp",EDGE,"E96");var subQ94=sQuery(id+"F6.wireOp",EDGE,"E94");var subQ95=sQuery(id+"F6.wireOp",EDGE,"E92");var subQ96=sQuery(id+"F6.wireOp",EDGE,"E90");var subQ97=sQuery(id+"F6.wireOp",EDGE,"E88");var subQ98=sQuery(id+"F6.wireOp",EDGE,"E86");var subQ99=sQuery(id+"F6.wireOp",EDGE,"E84");var subQ100=sQuery(id+"F6.wireOp",EDGE,"E82");var subQ101=sQuery(id+"F6.wireOp",EDGE,"E80");var subQ102=sQuery(id+"F6.wireOp",EDGE,"E78");var subQ103=sQuery(id+"F6.wireOp",EDGE,"E76");var subQ104=sQuery(id+"F6.wireOp",EDGE,"E72.MirrorCS");var subQ105=sQuery(id+"F6.wireOp",EDGE,"E71.MirrorCS");var subQ106=sQuery(id+"F6.wireOp",EDGE,"E70.MirrorCS");var subQ107=sQuery(id+"F6.wireOp",EDGE,"E67.MirrorCS");var subQ108=sQuery(id+"F6.wireOp",EDGE,"E59.MirrorCS");var subQ109=sQuery(id+"F6.wireOp",EDGE,"E58.MirrorCS");var subQ110=sQuery(id+"F6.wireOp",EDGE,"E57");var subQ111=sQuery(id+"F6.wireOp",EDGE,"E56");var subQ112=sQuery(id+"F6.wireOp",EDGE,"E55");var subQ113=sQuery(id+"F6.wireOp",EDGE,"E54");var subQ114=sQuery(id+"F6.wireOp",EDGE,"E50");var subQ115=sQuery(id+"F6.wireOp",EDGE,"E49");var subQ116=sQuery(id+"F6.wireOp",EDGE,"E48.MirrorCS");var subQ117=sQuery(id+"F6.wireOp",EDGE,"E47.MirrorCS");var subQ118=sQuery(id+"F6.wireOp",EDGE,"E34.MirrorCS");var subQ119=sQuery(id+"F6.wireOp",EDGE,"E33");var subQ120=sQuery(id+"F6.wireOp",EDGE,"E32");var subQ121=sQuery(id+"F6.wireOp",EDGE,"E31");var subQ122=sQuery(id+"F6.wireOp",EDGE,"E30");var subQ123=sQuery(id+"F6.wireOp",EDGE,"E29");var subQ124=sQuery(id+"F6.wireOp",EDGE,"E1.0");var subQ125=makeQuery(id+"F13.opExtrude","CAP_FACE",FACE,{"disambiguationData":[OSD([subQ124,subQ68,subQ63,subQ123,subQ122,subQ121,subQ120,subQ119,subQ118,subQ59,subQ55,subQ51,subQ47,subQ43,subQ39,subQ35,subQ31,subQ27,subQ18,subQ13,subQ2,subQ117,subQ116,subQ115,subQ114,subQ42,subQ67,subQ62,subQ113,subQ112,subQ111,subQ110,subQ109,subQ108,subQ58,subQ54,subQ50,subQ38,subQ34,subQ30,subQ26,subQ107,subQ12,subQ1,subQ106,subQ105,subQ104,subQ46,subQ17,subQ103,subQ102,subQ101,subQ100,subQ99,subQ98,subQ97,subQ96,subQ95,subQ94,subQ93,subQ92,subQ91,subQ90,subQ89,subQ88,subQ87,subQ86,subQ85,subQ84,subQ83,subQ82,subQ81,subQ80,subQ79,subQ25,subQ29,subQ33,subQ37,subQ41,subQ66,subQ61,subQ78,subQ77,subQ76,subQ75,subQ74,subQ73,subQ57,subQ53,subQ49,subQ45,subQ72,subQ71,subQ70,subQ0,subQ11,subQ16])],"isStart":true});var subQ126=makeQuery(id+"F14.opExtrude","CAP_FACE",FACE,{"disambiguationData":[OSD([subQ114,subQ107,sQuery(id+"F6.wireOp",EDGE,"E123"),subQ79])],"isStart":true});var subQ127=makeQuery(id+"F14.opExtrude","CAP_FACE",FACE,{"disambiguationData":[OSD([subQ119,subQ109,sQuery(id+"F6.wireOp",EDGE,"E99"),subQ74])],"isStart":true});var subQ129=makeQuery(id+"F14.opExtrude","CAP_FACE",FACE,{"disambiguationData":[OSD([subQ123,subQ113,sQuery(id+"F6.wireOp",EDGE,"E91"),subQ78])],"isStart":true});var subQ130=makeQuery(id+"F14.opExtrude","CAP_FACE",FACE,{"disambiguationData":[OSD([subQ122,subQ112,sQuery(id+"F6.wireOp",EDGE,"E93"),subQ77])],"isStart":true});var subQ131=makeQuery(id+"F17.opExtrude","CAP_FACE",FACE,{"disambiguationData":[OSD([subQ9,subQ8,subQ7,subQ6,subQ5,subQ4])],"isStart":true});var subQ132=makeQuery(id+"F14.opExtrude","CAP_FACE",FACE,{"disambiguationData":[OSD([subQ121,subQ111,sQuery(id+"F6.wireOp",EDGE,"E95"),subQ76])],"isStart":true});var subQ133=makeQuery(id+"F17.opExtrude","SWEPT_FACE",FACE,{"disambiguationData":[OSD([subQ7])]});var subQ139=makeQuery(id+"F13.opExtrude","CAP_FACE",FACE,{"disambiguationData":[OSD([subQ124,subQ68,subQ63,subQ123,subQ122,subQ121,subQ120,subQ119,subQ118,subQ59,subQ55,subQ51,subQ47,subQ43,subQ39,subQ35,subQ31,subQ27,subQ18,subQ13,subQ2,subQ117,subQ116,subQ115,subQ114,subQ42,subQ67,subQ62,subQ113,subQ112,subQ111,subQ110,subQ109,subQ108,subQ58,subQ54,subQ50,subQ38,subQ34,subQ30,subQ26,subQ107,subQ12,subQ1,subQ106,subQ105,subQ104,subQ46,subQ17,subQ103,subQ102,subQ101,subQ100,subQ99,subQ98,subQ97,subQ96,subQ95,subQ94,subQ93,subQ92,subQ91,subQ90,subQ89,subQ88,subQ87,subQ86,subQ85,subQ84,subQ83,subQ82,subQ81,subQ80,subQ79,subQ25,subQ29,subQ33,subQ37,subQ41,subQ66,subQ61,subQ78,subQ77,subQ76,subQ75,subQ74,subQ73,subQ57,subQ53,subQ49,subQ45,subQ72,subQ71,subQ70,subQ0,subQ11,subQ16])],"isStart":false});var subQ140=makeQuery(id+"F14.opExtrude","CAP_FACE",FACE,{"disambiguationData":[OSD([subQ120,subQ110,sQuery(id+"F6.wireOp",EDGE,"E97"),subQ75])],"isStart":true});var subQ141=makeQuery(id+"F17.opExtrude","SWEPT_FACE",FACE,{"disambiguationData":[OSD([subQ4])]});var subQ142=makeQuery(id+"F14.opExtrude","CAP_FACE",FACE,{"disambiguationData":[OSD([subQ118,subQ108,sQuery(id+"F6.wireOp",EDGE,"E101"),subQ73])],"isStart":true});var subQ143=makeQuery(id+"F14.opExtrude","CAP_FACE",FACE,{"disambiguationData":[OSD([subQ117,subQ106,sQuery(id+"F6.wireOp",EDGE,"E115"),subQ70])],"isStart":true});var subQ144=makeQuery(id+"F14.opExtrude","CAP_FACE",FACE,{"disambiguationData":[OSD([subQ116,subQ105,sQuery(id+"F6.wireOp",EDGE,"E113"),subQ71])],"isStart":true});var subQ145=makeQuery(id+"F14.opExtrude","CAP_FACE",FACE,{"disambiguationData":[OSD([subQ115,subQ104,sQuery(id+"F6.wireOp",EDGE,"E111"),subQ72])],"isStart":true});var subQ146=makeQuery(id+"F16.opRevolve","SWEPT_FACE",FACE,{"disambiguationData":[OSD([subQ20])]});var subQ147=makeQuery(id+"F17.opExtrude","SWEPT_FACE",FACE,{"disambiguationData":[OSD([subQ8])]});var subQ148=makeQuery(id+"F17.opExtrude","SWEPT_FACE",FACE,{"disambiguationData":[OSD([subQ5])]});Q0=makeQuery(id+"F19.boolean.opBoolean","INTERSECT",EDGE,{"derivedFrom":[makeQuery(id+"F18.boolean.opBoolean","SPLIT",FACE,{"disambiguationData":[TD([subQ15])],"derivedFrom":makeQuery(id+"F17.boolean.opBoolean","SPLIT",FACE,{"disambiguationData":[TD([makeQuery(id+"F13.opExtrude","SWEPT_FACE",FACE,{"disambiguationData":[OSD([subQ124])]}),subQ125,subQ139,subQ69,subQ64,subQ129,subQ130,subQ132,subQ140,subQ127,subQ142,subQ60,subQ56,subQ52,subQ48,subQ44,subQ40,subQ36,subQ32,subQ28,subQ19,subQ14,subQ3,subQ143,subQ144,subQ145,subQ126,subQ65,subQ24,subQ15,subQ146,subQ131,subQ10,subQ147,subQ133,subQ148,subQ141])],"derivedFrom":makeQuery(id+"F16.boolean.opBoolean","MERGE",FACE,{"derivedFrom":[makeQuery(id+"F15.opRevolve","SWEPT_FACE",FACE,{"disambiguationData":[OSD([subQ23])]}),makeQuery(id+"F16.opRevolve","SWEPT_FACE",FACE,{"disambiguationData":[OSD([subQ23])]})]})})}),makeQuery(id+"F19.opExtrude","SWEPT_FACE",FACE,{"disambiguationData":[OSD([sQuery(id+"F11.wireOp",EDGE,"E291.MirrorCS")])]})]});}
            var Q1;
            {var subQ0=sQuery(id+"F6.wireOp",EDGE,"E145");var subQ1=sQuery(id+"F6.wireOp",EDGE,"E69.MirrorCS");var subQ2=sQuery(id+"F6.wireOp",EDGE,"E46.MirrorCS");var subQ3=makeQuery(id+"F14.opExtrude","CAP_FACE",FACE,{"disambiguationData":[OSD([subQ2,subQ1,sQuery(id+"F6.wireOp",EDGE,"E117"),subQ0])],"isStart":true});var subQ4=sQuery(id+"F10.wireOp",EDGE,"E285");var subQ5=sQuery(id+"F10.wireOp",EDGE,"E284");var subQ6=sQuery(id+"F10.wireOp",EDGE,"E283");var subQ7=sQuery(id+"F10.wireOp",EDGE,"E282");var subQ8=sQuery(id+"F10.wireOp",EDGE,"E281");var subQ9=sQuery(id+"F10.wireOp",EDGE,"E280");var subQ10=makeQuery(id+"F17.opExtrude","CAP_FACE",FACE,{"disambiguationData":[OSD([subQ9,subQ8,subQ7,subQ6,subQ5,subQ4])],"isStart":false});var subQ11=sQuery(id+"F6.wireOp",EDGE,"E146");var subQ12=sQuery(id+"F6.wireOp",EDGE,"E68.MirrorCS");var subQ13=sQuery(id+"F6.wireOp",EDGE,"E45.MirrorCS");var subQ14=makeQuery(id+"F14.opExtrude","CAP_FACE",FACE,{"disambiguationData":[OSD([subQ13,subQ12,sQuery(id+"F6.wireOp",EDGE,"E120"),subQ11])],"isStart":true});var subQ15=makeQuery(id+"F16.opRevolve","SWEPT_FACE",FACE,{"disambiguationData":[OSD([sQuery(id+"F7.wireOp",EDGE,"E157")])]});var subQ16=sQuery(id+"F6.wireOp",EDGE,"E147");var subQ17=sQuery(id+"F6.wireOp",EDGE,"E74");var subQ18=sQuery(id+"F6.wireOp",EDGE,"E44.MirrorCS");var subQ19=makeQuery(id+"F14.opExtrude","CAP_FACE",FACE,{"disambiguationData":[OSD([subQ18,subQ17,sQuery(id+"F6.wireOp",EDGE,"E121"),subQ16])],"isStart":true});var subQ20=sQuery(id+"F7.wireOp",EDGE,"E164");var subQ21=sQuery(id+"F7.wireOp",EDGE,"E152");var subQ22=sQuery(id+"F7.wireOp",EDGE,"E151");var subQ23=sQuery(id+"F7.wireOp",EDGE,"E150");var subQ24=makeQuery(id+"F15.opRevolve","CAP_FACE",FACE,{"disambiguationData":[OSD([subQ23,subQ22,subQ21,subQ20])],"isStart":false});var subQ25=sQuery(id+"F6.wireOp",EDGE,"E125");var subQ26=sQuery(id+"F6.wireOp",EDGE,"E66.MirrorCS");var subQ27=sQuery(id+"F6.wireOp",EDGE,"E43.MirrorCS");var subQ28=makeQuery(id+"F14.opExtrude","CAP_FACE",FACE,{"disambiguationData":[OSD([subQ27,subQ26,sQuery(id+"F6.wireOp",EDGE,"E77"),subQ25])],"isStart":true});var subQ29=sQuery(id+"F6.wireOp",EDGE,"E126");var subQ30=sQuery(id+"F6.wireOp",EDGE,"E65.MirrorCS");var subQ31=sQuery(id+"F6.wireOp",EDGE,"E42.MirrorCS");var subQ32=makeQuery(id+"F14.opExtrude","CAP_FACE",FACE,{"disambiguationData":[OSD([subQ31,subQ30,sQuery(id+"F6.wireOp",EDGE,"E79"),subQ29])],"isStart":true});var subQ33=sQuery(id+"F6.wireOp",EDGE,"E127");var subQ34=sQuery(id+"F6.wireOp",EDGE,"E64.MirrorCS");var subQ35=sQuery(id+"F6.wireOp",EDGE,"E41.MirrorCS");var subQ36=makeQuery(id+"F14.opExtrude","CAP_FACE",FACE,{"disambiguationData":[OSD([subQ35,subQ34,sQuery(id+"F6.wireOp",EDGE,"E81"),subQ33])],"isStart":true});var subQ37=sQuery(id+"F6.wireOp",EDGE,"E128");var subQ38=sQuery(id+"F6.wireOp",EDGE,"E63.MirrorCS");var subQ39=sQuery(id+"F6.wireOp",EDGE,"E40.MirrorCS");var subQ40=makeQuery(id+"F14.opExtrude","CAP_FACE",FACE,{"disambiguationData":[OSD([subQ39,subQ38,sQuery(id+"F6.wireOp",EDGE,"E83"),subQ37])],"isStart":true});var subQ41=sQuery(id+"F6.wireOp",EDGE,"E129");var subQ42=sQuery(id+"F6.wireOp",EDGE,"E51");var subQ43=sQuery(id+"F6.wireOp",EDGE,"E39.MirrorCS");var subQ44=makeQuery(id+"F14.opExtrude","CAP_FACE",FACE,{"disambiguationData":[OSD([subQ43,subQ42,sQuery(id+"F6.wireOp",EDGE,"E85"),subQ41])],"isStart":true});var subQ45=sQuery(id+"F6.wireOp",EDGE,"E141");var subQ46=sQuery(id+"F6.wireOp",EDGE,"E73");var subQ47=sQuery(id+"F6.wireOp",EDGE,"E38.MirrorCS");var subQ48=makeQuery(id+"F14.opExtrude","CAP_FACE",FACE,{"disambiguationData":[OSD([subQ47,subQ46,sQuery(id+"F6.wireOp",EDGE,"E109"),subQ45])],"isStart":true});var subQ49=sQuery(id+"F6.wireOp",EDGE,"E140");var subQ50=sQuery(id+"F6.wireOp",EDGE,"E62.MirrorCS");var subQ51=sQuery(id+"F6.wireOp",EDGE,"E37.MirrorCS");var subQ52=makeQuery(id+"F14.opExtrude","CAP_FACE",FACE,{"disambiguationData":[OSD([subQ51,subQ50,sQuery(id+"F6.wireOp",EDGE,"E107"),subQ49])],"isStart":true});var subQ53=sQuery(id+"F6.wireOp",EDGE,"E139");var subQ54=sQuery(id+"F6.wireOp",EDGE,"E61.MirrorCS");var subQ55=sQuery(id+"F6.wireOp",EDGE,"E36.MirrorCS");var subQ56=makeQuery(id+"F14.opExtrude","CAP_FACE",FACE,{"disambiguationData":[OSD([subQ55,subQ54,sQuery(id+"F6.wireOp",EDGE,"E105"),subQ53])],"isStart":true});var subQ57=sQuery(id+"F6.wireOp",EDGE,"E138");var subQ58=sQuery(id+"F6.wireOp",EDGE,"E60.MirrorCS");var subQ59=sQuery(id+"F6.wireOp",EDGE,"E35.MirrorCS");var subQ60=makeQuery(id+"F14.opExtrude","CAP_FACE",FACE,{"disambiguationData":[OSD([subQ59,subQ58,sQuery(id+"F6.wireOp",EDGE,"E103"),subQ57])],"isStart":true});var subQ61=sQuery(id+"F6.wireOp",EDGE,"E131");var subQ62=sQuery(id+"F6.wireOp",EDGE,"E53");var subQ63=sQuery(id+"F6.wireOp",EDGE,"E28");var subQ64=makeQuery(id+"F14.opExtrude","CAP_FACE",FACE,{"disambiguationData":[OSD([subQ63,subQ62,sQuery(id+"F6.wireOp",EDGE,"E89"),subQ61])],"isStart":true});var subQ65=makeQuery(id+"F15.opRevolve","CAP_FACE",FACE,{"disambiguationData":[OSD([subQ23,subQ22,subQ21,subQ20])],"isStart":true});var subQ66=sQuery(id+"F6.wireOp",EDGE,"E130");var subQ67=sQuery(id+"F6.wireOp",EDGE,"E52");var subQ68=sQuery(id+"F6.wireOp",EDGE,"E27");var subQ69=makeQuery(id+"F14.opExtrude","CAP_FACE",FACE,{"disambiguationData":[OSD([subQ68,subQ67,sQuery(id+"F6.wireOp",EDGE,"E87"),subQ66])],"isStart":true});var subQ70=sQuery(id+"F6.wireOp",EDGE,"E144");var subQ71=sQuery(id+"F6.wireOp",EDGE,"E143");var subQ72=sQuery(id+"F6.wireOp",EDGE,"E142");var subQ73=sQuery(id+"F6.wireOp",EDGE,"E137");var subQ74=sQuery(id+"F6.wireOp",EDGE,"E136");var subQ75=sQuery(id+"F6.wireOp",EDGE,"E135");var subQ76=sQuery(id+"F6.wireOp",EDGE,"E134");var subQ77=sQuery(id+"F6.wireOp",EDGE,"E133");var subQ78=sQuery(id+"F6.wireOp",EDGE,"E132");var subQ79=sQuery(id+"F6.wireOp",EDGE,"E124");var subQ80=sQuery(id+"F6.wireOp",EDGE,"E122");var subQ81=sQuery(id+"F6.wireOp",EDGE,"E119");var subQ82=sQuery(id+"F6.wireOp",EDGE,"E118");var subQ83=sQuery(id+"F6.wireOp",EDGE,"E116");var subQ84=sQuery(id+"F6.wireOp",EDGE,"E114");var subQ85=sQuery(id+"F6.wireOp",EDGE,"E112");var subQ86=sQuery(id+"F6.wireOp",EDGE,"E110");var subQ87=sQuery(id+"F6.wireOp",EDGE,"E108");var subQ88=sQuery(id+"F6.wireOp",EDGE,"E106");var subQ89=sQuery(id+"F6.wireOp",EDGE,"E104");var subQ90=sQuery(id+"F6.wireOp",EDGE,"E102");var subQ91=sQuery(id+"F6.wireOp",EDGE,"E100");var subQ92=sQuery(id+"F6.wireOp",EDGE,"E98");var subQ93=sQuery(id+"F6.wireOp",EDGE,"E96");var subQ94=sQuery(id+"F6.wireOp",EDGE,"E94");var subQ95=sQuery(id+"F6.wireOp",EDGE,"E92");var subQ96=sQuery(id+"F6.wireOp",EDGE,"E90");var subQ97=sQuery(id+"F6.wireOp",EDGE,"E88");var subQ98=sQuery(id+"F6.wireOp",EDGE,"E86");var subQ99=sQuery(id+"F6.wireOp",EDGE,"E84");var subQ100=sQuery(id+"F6.wireOp",EDGE,"E82");var subQ101=sQuery(id+"F6.wireOp",EDGE,"E80");var subQ102=sQuery(id+"F6.wireOp",EDGE,"E78");var subQ103=sQuery(id+"F6.wireOp",EDGE,"E76");var subQ104=sQuery(id+"F6.wireOp",EDGE,"E72.MirrorCS");var subQ105=sQuery(id+"F6.wireOp",EDGE,"E71.MirrorCS");var subQ106=sQuery(id+"F6.wireOp",EDGE,"E70.MirrorCS");var subQ107=sQuery(id+"F6.wireOp",EDGE,"E67.MirrorCS");var subQ108=sQuery(id+"F6.wireOp",EDGE,"E59.MirrorCS");var subQ109=sQuery(id+"F6.wireOp",EDGE,"E58.MirrorCS");var subQ110=sQuery(id+"F6.wireOp",EDGE,"E57");var subQ111=sQuery(id+"F6.wireOp",EDGE,"E56");var subQ112=sQuery(id+"F6.wireOp",EDGE,"E55");var subQ113=sQuery(id+"F6.wireOp",EDGE,"E54");var subQ114=sQuery(id+"F6.wireOp",EDGE,"E50");var subQ115=sQuery(id+"F6.wireOp",EDGE,"E49");var subQ116=sQuery(id+"F6.wireOp",EDGE,"E48.MirrorCS");var subQ117=sQuery(id+"F6.wireOp",EDGE,"E47.MirrorCS");var subQ118=sQuery(id+"F6.wireOp",EDGE,"E34.MirrorCS");var subQ119=sQuery(id+"F6.wireOp",EDGE,"E33");var subQ120=sQuery(id+"F6.wireOp",EDGE,"E32");var subQ121=sQuery(id+"F6.wireOp",EDGE,"E31");var subQ122=sQuery(id+"F6.wireOp",EDGE,"E30");var subQ123=sQuery(id+"F6.wireOp",EDGE,"E29");var subQ124=sQuery(id+"F6.wireOp",EDGE,"E1.0");var subQ125=makeQuery(id+"F13.opExtrude","CAP_FACE",FACE,{"disambiguationData":[OSD([subQ124,subQ68,subQ63,subQ123,subQ122,subQ121,subQ120,subQ119,subQ118,subQ59,subQ55,subQ51,subQ47,subQ43,subQ39,subQ35,subQ31,subQ27,subQ18,subQ13,subQ2,subQ117,subQ116,subQ115,subQ114,subQ42,subQ67,subQ62,subQ113,subQ112,subQ111,subQ110,subQ109,subQ108,subQ58,subQ54,subQ50,subQ38,subQ34,subQ30,subQ26,subQ107,subQ12,subQ1,subQ106,subQ105,subQ104,subQ46,subQ17,subQ103,subQ102,subQ101,subQ100,subQ99,subQ98,subQ97,subQ96,subQ95,subQ94,subQ93,subQ92,subQ91,subQ90,subQ89,subQ88,subQ87,subQ86,subQ85,subQ84,subQ83,subQ82,subQ81,subQ80,subQ79,subQ25,subQ29,subQ33,subQ37,subQ41,subQ66,subQ61,subQ78,subQ77,subQ76,subQ75,subQ74,subQ73,subQ57,subQ53,subQ49,subQ45,subQ72,subQ71,subQ70,subQ0,subQ11,subQ16])],"isStart":true});var subQ126=makeQuery(id+"F14.opExtrude","CAP_FACE",FACE,{"disambiguationData":[OSD([subQ114,subQ107,sQuery(id+"F6.wireOp",EDGE,"E123"),subQ79])],"isStart":true});var subQ127=makeQuery(id+"F14.opExtrude","CAP_FACE",FACE,{"disambiguationData":[OSD([subQ119,subQ109,sQuery(id+"F6.wireOp",EDGE,"E99"),subQ74])],"isStart":true});var subQ129=makeQuery(id+"F14.opExtrude","CAP_FACE",FACE,{"disambiguationData":[OSD([subQ123,subQ113,sQuery(id+"F6.wireOp",EDGE,"E91"),subQ78])],"isStart":true});var subQ130=makeQuery(id+"F14.opExtrude","CAP_FACE",FACE,{"disambiguationData":[OSD([subQ122,subQ112,sQuery(id+"F6.wireOp",EDGE,"E93"),subQ77])],"isStart":true});var subQ131=makeQuery(id+"F17.opExtrude","CAP_FACE",FACE,{"disambiguationData":[OSD([subQ9,subQ8,subQ7,subQ6,subQ5,subQ4])],"isStart":true});var subQ132=makeQuery(id+"F14.opExtrude","CAP_FACE",FACE,{"disambiguationData":[OSD([subQ121,subQ111,sQuery(id+"F6.wireOp",EDGE,"E95"),subQ76])],"isStart":true});var subQ133=makeQuery(id+"F17.opExtrude","SWEPT_FACE",FACE,{"disambiguationData":[OSD([subQ7])]});var subQ139=makeQuery(id+"F13.opExtrude","CAP_FACE",FACE,{"disambiguationData":[OSD([subQ124,subQ68,subQ63,subQ123,subQ122,subQ121,subQ120,subQ119,subQ118,subQ59,subQ55,subQ51,subQ47,subQ43,subQ39,subQ35,subQ31,subQ27,subQ18,subQ13,subQ2,subQ117,subQ116,subQ115,subQ114,subQ42,subQ67,subQ62,subQ113,subQ112,subQ111,subQ110,subQ109,subQ108,subQ58,subQ54,subQ50,subQ38,subQ34,subQ30,subQ26,subQ107,subQ12,subQ1,subQ106,subQ105,subQ104,subQ46,subQ17,subQ103,subQ102,subQ101,subQ100,subQ99,subQ98,subQ97,subQ96,subQ95,subQ94,subQ93,subQ92,subQ91,subQ90,subQ89,subQ88,subQ87,subQ86,subQ85,subQ84,subQ83,subQ82,subQ81,subQ80,subQ79,subQ25,subQ29,subQ33,subQ37,subQ41,subQ66,subQ61,subQ78,subQ77,subQ76,subQ75,subQ74,subQ73,subQ57,subQ53,subQ49,subQ45,subQ72,subQ71,subQ70,subQ0,subQ11,subQ16])],"isStart":false});var subQ140=makeQuery(id+"F14.opExtrude","CAP_FACE",FACE,{"disambiguationData":[OSD([subQ120,subQ110,sQuery(id+"F6.wireOp",EDGE,"E97"),subQ75])],"isStart":true});var subQ141=makeQuery(id+"F17.opExtrude","SWEPT_FACE",FACE,{"disambiguationData":[OSD([subQ4])]});var subQ142=makeQuery(id+"F14.opExtrude","CAP_FACE",FACE,{"disambiguationData":[OSD([subQ118,subQ108,sQuery(id+"F6.wireOp",EDGE,"E101"),subQ73])],"isStart":true});var subQ143=makeQuery(id+"F14.opExtrude","CAP_FACE",FACE,{"disambiguationData":[OSD([subQ117,subQ106,sQuery(id+"F6.wireOp",EDGE,"E115"),subQ70])],"isStart":true});var subQ144=makeQuery(id+"F14.opExtrude","CAP_FACE",FACE,{"disambiguationData":[OSD([subQ116,subQ105,sQuery(id+"F6.wireOp",EDGE,"E113"),subQ71])],"isStart":true});var subQ145=makeQuery(id+"F14.opExtrude","CAP_FACE",FACE,{"disambiguationData":[OSD([subQ115,subQ104,sQuery(id+"F6.wireOp",EDGE,"E111"),subQ72])],"isStart":true});var subQ146=makeQuery(id+"F16.opRevolve","SWEPT_FACE",FACE,{"disambiguationData":[OSD([subQ20])]});var subQ147=makeQuery(id+"F17.opExtrude","SWEPT_FACE",FACE,{"disambiguationData":[OSD([subQ8])]});var subQ148=makeQuery(id+"F17.opExtrude","SWEPT_FACE",FACE,{"disambiguationData":[OSD([subQ5])]});Q1=makeQuery(id+"F19.boolean.opBoolean","INTERSECT",EDGE,{"derivedFrom":[makeQuery(id+"F18.boolean.opBoolean","SPLIT",FACE,{"disambiguationData":[TD([subQ15])],"derivedFrom":makeQuery(id+"F17.boolean.opBoolean","SPLIT",FACE,{"disambiguationData":[TD([makeQuery(id+"F13.opExtrude","SWEPT_FACE",FACE,{"disambiguationData":[OSD([subQ124])]}),subQ125,subQ139,subQ69,subQ64,subQ129,subQ130,subQ132,subQ140,subQ127,subQ142,subQ60,subQ56,subQ52,subQ48,subQ44,subQ40,subQ36,subQ32,subQ28,subQ19,subQ14,subQ3,subQ143,subQ144,subQ145,subQ126,subQ65,subQ24,subQ15,subQ146,subQ131,subQ10,subQ147,subQ133,subQ148,subQ141])],"derivedFrom":makeQuery(id+"F16.boolean.opBoolean","MERGE",FACE,{"derivedFrom":[makeQuery(id+"F15.opRevolve","SWEPT_FACE",FACE,{"disambiguationData":[OSD([subQ23])]}),makeQuery(id+"F16.opRevolve","SWEPT_FACE",FACE,{"disambiguationData":[OSD([subQ23])]})]})})}),makeQuery(id+"F19.opExtrude","SWEPT_FACE",FACE,{"disambiguationData":[OSD([sQuery(id+"F11.wireOp",EDGE,"E290.MirrorCS")])]})]});}
            fillet(context, id + "F27", {"entities" : qUnion([Q0, Q1]), "radius" : 5 * mm, "tangentPropagation" : true, "allowEdgeOverflow" : false});
        }
        {
            var Q0;
            Q0=makeQuery(id+"F22.boolean.opBoolean","MERGE",EDGE,{"derivedFrom":[makeQuery(id+"F21.opExtrude","SWEPT_EDGE",EDGE,{"disambiguationData":[OSD([sQuery(id+"F11.wireOp",EDGE,"E302"),sQuery(id+"F11.wireOp",EDGE,"E303")])]}),makeQuery(id+"F22.opExtrude","SWEPT_EDGE",EDGE,{"disambiguationData":[OSD([sQuery(id+"F12.wireOp",EDGE,"E320"),sQuery(id+"F12.wireOp",EDGE,"E321")])]})]});
            var Q1;
            Q1=makeQuery(id+"F22.boolean.opBoolean","MERGE",EDGE,{"derivedFrom":[makeQuery(id+"F21.opExtrude","SWEPT_EDGE",EDGE,{"disambiguationData":[OSD([sQuery(id+"F11.wireOp",EDGE,"E303"),sQuery(id+"F11.wireOp",EDGE,"E304")])]}),makeQuery(id+"F22.opExtrude","SWEPT_EDGE",EDGE,{"disambiguationData":[OSD([sQuery(id+"F12.wireOp",EDGE,"E321"),sQuery(id+"F12.wireOp",EDGE,"E322")])]})]});
            var Q2;
            Q2=makeQuery(id+"F22.opExtrude","SWEPT_EDGE",EDGE,{"disambiguationData":[OSD([sQuery(id+"F12.wireOp",EDGE,"E309.MirrorCS"),sQuery(id+"F12.wireOp",EDGE,"E324.0")])]});
            var Q3;
            Q3=makeQuery(id+"F22.opExtrude","SWEPT_EDGE",EDGE,{"disambiguationData":[OSD([sQuery(id+"F12.wireOp",EDGE,"E308.MirrorCS"),sQuery(id+"F12.wireOp",EDGE,"E324.0")])]});
            var Q4;
            Q4=makeQuery(id+"F21.opExtrude","CAP_EDGE",EDGE,{"disambiguationData":[OSD([sQuery(id+"F11.wireOp",EDGE,"E303")])],"isStart":true});
            var Q5;
            Q5=makeQuery(id+"F21.opExtrude","CAP_EDGE",EDGE,{"disambiguationData":[OSD([sQuery(id+"F11.wireOp",EDGE,"E304")])],"isStart":true});
            var Q6;
            Q6=makeQuery(id+"F21.opExtrude","CAP_EDGE",EDGE,{"disambiguationData":[OSD([sQuery(id+"F11.wireOp",EDGE,"E302")])],"isStart":true});
            var Q7;
            {var subQ3=sQuery(id+"F9.wireOp",EDGE,"E256");var subQ4=sQuery(id+"F9.wireOp",EDGE,"E255");var subQ8=sQuery(id+"F7.wireOp",EDGE,"E150");var subQ9=makeQuery(id+"F16.opRevolve","SWEPT_FACE",FACE,{"disambiguationData":[OSD([subQ8])]});var subQ10=makeQuery(id+"F15.opRevolve","SWEPT_FACE",FACE,{"disambiguationData":[OSD([subQ8])]});var subQ11=makeQuery(id+"F18.opExtrude","SWEPT_FACE",FACE,{"disambiguationData":[OSD([subQ4])]});var subQ12=makeQuery(id+"F19.opExtrude","SWEPT_FACE",FACE,{"disambiguationData":[OSD([sQuery(id+"F11.wireOp",EDGE,"E291.MirrorCS")])]});var subQ13=sQuery(id+"F11.wireOp",EDGE,"E304");var subQ14=makeQuery(id+"F18.opExtrude","SWEPT_FACE",FACE,{"disambiguationData":[OSD([subQ3])]});var subQ15=sQuery(id+"F10.wireOp",EDGE,"E282");var subQ16=makeQuery(id+"F17.opExtrude","SWEPT_FACE",FACE,{"disambiguationData":[OSD([subQ15])]});var subQ17=sQuery(id+"F6.wireOp",EDGE,"E145");var subQ18=sQuery(id+"F6.wireOp",EDGE,"E69.MirrorCS");var subQ19=sQuery(id+"F6.wireOp",EDGE,"E46.MirrorCS");var subQ20=makeQuery(id+"F14.opExtrude","CAP_FACE",FACE,{"disambiguationData":[OSD([subQ19,subQ18,sQuery(id+"F6.wireOp",EDGE,"E117"),subQ17])],"isStart":true});var subQ21=sQuery(id+"F10.wireOp",EDGE,"E285");var subQ22=sQuery(id+"F10.wireOp",EDGE,"E284");var subQ23=sQuery(id+"F10.wireOp",EDGE,"E283");var subQ24=sQuery(id+"F10.wireOp",EDGE,"E281");var subQ25=sQuery(id+"F10.wireOp",EDGE,"E280");var subQ26=makeQuery(id+"F17.opExtrude","CAP_FACE",FACE,{"disambiguationData":[OSD([subQ25,subQ24,subQ15,subQ23,subQ22,subQ21])],"isStart":false});var subQ27=sQuery(id+"F6.wireOp",EDGE,"E146");var subQ28=sQuery(id+"F6.wireOp",EDGE,"E68.MirrorCS");var subQ29=sQuery(id+"F6.wireOp",EDGE,"E45.MirrorCS");var subQ30=makeQuery(id+"F14.opExtrude","CAP_FACE",FACE,{"disambiguationData":[OSD([subQ29,subQ28,sQuery(id+"F6.wireOp",EDGE,"E120"),subQ27])],"isStart":true});var subQ31=makeQuery(id+"F16.opRevolve","SWEPT_FACE",FACE,{"disambiguationData":[OSD([sQuery(id+"F7.wireOp",EDGE,"E157")])]});var subQ32=sQuery(id+"F6.wireOp",EDGE,"E147");var subQ33=sQuery(id+"F6.wireOp",EDGE,"E74");var subQ34=sQuery(id+"F6.wireOp",EDGE,"E44.MirrorCS");var subQ35=makeQuery(id+"F14.opExtrude","CAP_FACE",FACE,{"disambiguationData":[OSD([subQ34,subQ33,sQuery(id+"F6.wireOp",EDGE,"E121"),subQ32])],"isStart":true});var subQ36=sQuery(id+"F7.wireOp",EDGE,"E164");var subQ37=sQuery(id+"F7.wireOp",EDGE,"E152");var subQ38=sQuery(id+"F7.wireOp",EDGE,"E151");var subQ39=makeQuery(id+"F15.opRevolve","CAP_FACE",FACE,{"disambiguationData":[OSD([subQ8,subQ38,subQ37,subQ36])],"isStart":false});var subQ40=sQuery(id+"F6.wireOp",EDGE,"E125");var subQ41=sQuery(id+"F6.wireOp",EDGE,"E66.MirrorCS");var subQ42=sQuery(id+"F6.wireOp",EDGE,"E43.MirrorCS");var subQ43=makeQuery(id+"F14.opExtrude","CAP_FACE",FACE,{"disambiguationData":[OSD([subQ42,subQ41,sQuery(id+"F6.wireOp",EDGE,"E77"),subQ40])],"isStart":true});var subQ44=sQuery(id+"F6.wireOp",EDGE,"E126");var subQ45=sQuery(id+"F6.wireOp",EDGE,"E65.MirrorCS");var subQ46=sQuery(id+"F6.wireOp",EDGE,"E42.MirrorCS");var subQ47=makeQuery(id+"F14.opExtrude","CAP_FACE",FACE,{"disambiguationData":[OSD([subQ46,subQ45,sQuery(id+"F6.wireOp",EDGE,"E79"),subQ44])],"isStart":true});var subQ48=sQuery(id+"F6.wireOp",EDGE,"E127");var subQ49=sQuery(id+"F6.wireOp",EDGE,"E64.MirrorCS");var subQ50=sQuery(id+"F6.wireOp",EDGE,"E41.MirrorCS");var subQ51=makeQuery(id+"F14.opExtrude","CAP_FACE",FACE,{"disambiguationData":[OSD([subQ50,subQ49,sQuery(id+"F6.wireOp",EDGE,"E81"),subQ48])],"isStart":true});var subQ52=sQuery(id+"F6.wireOp",EDGE,"E128");var subQ53=sQuery(id+"F6.wireOp",EDGE,"E63.MirrorCS");var subQ54=sQuery(id+"F6.wireOp",EDGE,"E40.MirrorCS");var subQ55=makeQuery(id+"F14.opExtrude","CAP_FACE",FACE,{"disambiguationData":[OSD([subQ54,subQ53,sQuery(id+"F6.wireOp",EDGE,"E83"),subQ52])],"isStart":true});var subQ56=sQuery(id+"F6.wireOp",EDGE,"E129");var subQ57=sQuery(id+"F6.wireOp",EDGE,"E51");var subQ58=sQuery(id+"F6.wireOp",EDGE,"E39.MirrorCS");var subQ59=makeQuery(id+"F14.opExtrude","CAP_FACE",FACE,{"disambiguationData":[OSD([subQ58,subQ57,sQuery(id+"F6.wireOp",EDGE,"E85"),subQ56])],"isStart":true});var subQ60=sQuery(id+"F6.wireOp",EDGE,"E141");var subQ61=sQuery(id+"F6.wireOp",EDGE,"E73");var subQ62=sQuery(id+"F6.wireOp",EDGE,"E38.MirrorCS");var subQ63=makeQuery(id+"F14.opExtrude","CAP_FACE",FACE,{"disambiguationData":[OSD([subQ62,subQ61,sQuery(id+"F6.wireOp",EDGE,"E109"),subQ60])],"isStart":true});var subQ64=sQuery(id+"F6.wireOp",EDGE,"E140");var subQ65=sQuery(id+"F6.wireOp",EDGE,"E62.MirrorCS");var subQ66=sQuery(id+"F6.wireOp",EDGE,"E37.MirrorCS");var subQ67=makeQuery(id+"F14.opExtrude","CAP_FACE",FACE,{"disambiguationData":[OSD([subQ66,subQ65,sQuery(id+"F6.wireOp",EDGE,"E107"),subQ64])],"isStart":true});var subQ68=sQuery(id+"F6.wireOp",EDGE,"E139");var subQ69=sQuery(id+"F6.wireOp",EDGE,"E61.MirrorCS");var subQ70=sQuery(id+"F6.wireOp",EDGE,"E36.MirrorCS");var subQ71=makeQuery(id+"F14.opExtrude","CAP_FACE",FACE,{"disambiguationData":[OSD([subQ70,subQ69,sQuery(id+"F6.wireOp",EDGE,"E105"),subQ68])],"isStart":true});var subQ72=sQuery(id+"F6.wireOp",EDGE,"E138");var subQ73=sQuery(id+"F6.wireOp",EDGE,"E60.MirrorCS");var subQ74=sQuery(id+"F6.wireOp",EDGE,"E35.MirrorCS");var subQ75=makeQuery(id+"F14.opExtrude","CAP_FACE",FACE,{"disambiguationData":[OSD([subQ74,subQ73,sQuery(id+"F6.wireOp",EDGE,"E103"),subQ72])],"isStart":true});var subQ76=sQuery(id+"F6.wireOp",EDGE,"E131");var subQ77=sQuery(id+"F6.wireOp",EDGE,"E53");var subQ78=sQuery(id+"F6.wireOp",EDGE,"E28");var subQ79=makeQuery(id+"F14.opExtrude","CAP_FACE",FACE,{"disambiguationData":[OSD([subQ78,subQ77,sQuery(id+"F6.wireOp",EDGE,"E89"),subQ76])],"isStart":true});var subQ80=makeQuery(id+"F15.opRevolve","CAP_FACE",FACE,{"disambiguationData":[OSD([subQ8,subQ38,subQ37,subQ36])],"isStart":true});var subQ81=sQuery(id+"F6.wireOp",EDGE,"E130");var subQ82=sQuery(id+"F6.wireOp",EDGE,"E52");var subQ83=sQuery(id+"F6.wireOp",EDGE,"E27");var subQ84=makeQuery(id+"F14.opExtrude","CAP_FACE",FACE,{"disambiguationData":[OSD([subQ83,subQ82,sQuery(id+"F6.wireOp",EDGE,"E87"),subQ81])],"isStart":true});var subQ85=sQuery(id+"F6.wireOp",EDGE,"E144");var subQ86=sQuery(id+"F6.wireOp",EDGE,"E143");var subQ87=sQuery(id+"F6.wireOp",EDGE,"E142");var subQ88=sQuery(id+"F6.wireOp",EDGE,"E137");var subQ89=sQuery(id+"F6.wireOp",EDGE,"E136");var subQ90=sQuery(id+"F6.wireOp",EDGE,"E135");var subQ91=sQuery(id+"F6.wireOp",EDGE,"E134");var subQ92=sQuery(id+"F6.wireOp",EDGE,"E133");var subQ93=sQuery(id+"F6.wireOp",EDGE,"E132");var subQ94=sQuery(id+"F6.wireOp",EDGE,"E124");var subQ95=sQuery(id+"F6.wireOp",EDGE,"E122");var subQ96=sQuery(id+"F6.wireOp",EDGE,"E119");var subQ97=sQuery(id+"F6.wireOp",EDGE,"E118");var subQ98=sQuery(id+"F6.wireOp",EDGE,"E116");var subQ99=sQuery(id+"F6.wireOp",EDGE,"E114");var subQ100=sQuery(id+"F6.wireOp",EDGE,"E112");var subQ101=sQuery(id+"F6.wireOp",EDGE,"E110");var subQ102=sQuery(id+"F6.wireOp",EDGE,"E108");var subQ103=sQuery(id+"F6.wireOp",EDGE,"E106");var subQ104=sQuery(id+"F6.wireOp",EDGE,"E104");var subQ105=sQuery(id+"F6.wireOp",EDGE,"E102");var subQ106=sQuery(id+"F6.wireOp",EDGE,"E100");var subQ107=sQuery(id+"F6.wireOp",EDGE,"E98");var subQ108=sQuery(id+"F6.wireOp",EDGE,"E96");var subQ109=sQuery(id+"F6.wireOp",EDGE,"E94");var subQ110=sQuery(id+"F6.wireOp",EDGE,"E92");var subQ111=sQuery(id+"F6.wireOp",EDGE,"E90");var subQ112=sQuery(id+"F6.wireOp",EDGE,"E88");var subQ113=sQuery(id+"F6.wireOp",EDGE,"E86");var subQ114=sQuery(id+"F6.wireOp",EDGE,"E84");var subQ115=sQuery(id+"F6.wireOp",EDGE,"E82");var subQ116=sQuery(id+"F6.wireOp",EDGE,"E80");var subQ117=sQuery(id+"F6.wireOp",EDGE,"E78");var subQ118=sQuery(id+"F6.wireOp",EDGE,"E76");var subQ119=sQuery(id+"F6.wireOp",EDGE,"E72.MirrorCS");var subQ120=sQuery(id+"F6.wireOp",EDGE,"E71.MirrorCS");var subQ121=sQuery(id+"F6.wireOp",EDGE,"E70.MirrorCS");var subQ122=sQuery(id+"F6.wireOp",EDGE,"E67.MirrorCS");var subQ123=sQuery(id+"F6.wireOp",EDGE,"E59.MirrorCS");var subQ124=sQuery(id+"F6.wireOp",EDGE,"E58.MirrorCS");var subQ125=sQuery(id+"F6.wireOp",EDGE,"E57");var subQ126=sQuery(id+"F6.wireOp",EDGE,"E56");var subQ127=sQuery(id+"F6.wireOp",EDGE,"E55");var subQ128=sQuery(id+"F6.wireOp",EDGE,"E54");var subQ129=sQuery(id+"F6.wireOp",EDGE,"E50");var subQ130=sQuery(id+"F6.wireOp",EDGE,"E49");var subQ131=sQuery(id+"F6.wireOp",EDGE,"E48.MirrorCS");var subQ132=sQuery(id+"F6.wireOp",EDGE,"E47.MirrorCS");var subQ133=sQuery(id+"F6.wireOp",EDGE,"E34.MirrorCS");var subQ134=sQuery(id+"F6.wireOp",EDGE,"E33");var subQ135=sQuery(id+"F6.wireOp",EDGE,"E32");var subQ136=sQuery(id+"F6.wireOp",EDGE,"E31");var subQ137=sQuery(id+"F6.wireOp",EDGE,"E30");var subQ138=sQuery(id+"F6.wireOp",EDGE,"E29");var subQ139=sQuery(id+"F6.wireOp",EDGE,"E1.0");var subQ140=makeQuery(id+"F13.opExtrude","CAP_FACE",FACE,{"disambiguationData":[OSD([subQ139,subQ83,subQ78,subQ138,subQ137,subQ136,subQ135,subQ134,subQ133,subQ74,subQ70,subQ66,subQ62,subQ58,subQ54,subQ50,subQ46,subQ42,subQ34,subQ29,subQ19,subQ132,subQ131,subQ130,subQ129,subQ57,subQ82,subQ77,subQ128,subQ127,subQ126,subQ125,subQ124,subQ123,subQ73,subQ69,subQ65,subQ53,subQ49,subQ45,subQ41,subQ122,subQ28,subQ18,subQ121,subQ120,subQ119,subQ61,subQ33,subQ118,subQ117,subQ116,subQ115,subQ114,subQ113,subQ112,subQ111,subQ110,subQ109,subQ108,subQ107,subQ106,subQ105,subQ104,subQ103,subQ102,subQ101,subQ100,subQ99,subQ98,subQ97,subQ96,subQ95,subQ94,subQ40,subQ44,subQ48,subQ52,subQ56,subQ81,subQ76,subQ93,subQ92,subQ91,subQ90,subQ89,subQ88,subQ72,subQ68,subQ64,subQ60,subQ87,subQ86,subQ85,subQ17,subQ27,subQ32])],"isStart":true});var subQ141=makeQuery(id+"F14.opExtrude","CAP_FACE",FACE,{"disambiguationData":[OSD([subQ129,subQ122,sQuery(id+"F6.wireOp",EDGE,"E123"),subQ94])],"isStart":true});var subQ142=makeQuery(id+"F14.opExtrude","CAP_FACE",FACE,{"disambiguationData":[OSD([subQ134,subQ124,sQuery(id+"F6.wireOp",EDGE,"E99"),subQ89])],"isStart":true});var subQ143=makeQuery(id+"F14.opExtrude","CAP_FACE",FACE,{"disambiguationData":[OSD([subQ138,subQ128,sQuery(id+"F6.wireOp",EDGE,"E91"),subQ93])],"isStart":true});var subQ144=makeQuery(id+"F14.opExtrude","CAP_FACE",FACE,{"disambiguationData":[OSD([subQ137,subQ127,sQuery(id+"F6.wireOp",EDGE,"E93"),subQ92])],"isStart":true});var subQ145=makeQuery(id+"F17.opExtrude","CAP_FACE",FACE,{"disambiguationData":[OSD([subQ25,subQ24,subQ15,subQ23,subQ22,subQ21])],"isStart":true});var subQ146=makeQuery(id+"F14.opExtrude","CAP_FACE",FACE,{"disambiguationData":[OSD([subQ136,subQ126,sQuery(id+"F6.wireOp",EDGE,"E95"),subQ91])],"isStart":true});var subQ147=makeQuery(id+"F13.opExtrude","CAP_FACE",FACE,{"disambiguationData":[OSD([subQ139,subQ83,subQ78,subQ138,subQ137,subQ136,subQ135,subQ134,subQ133,subQ74,subQ70,subQ66,subQ62,subQ58,subQ54,subQ50,subQ46,subQ42,subQ34,subQ29,subQ19,subQ132,subQ131,subQ130,subQ129,subQ57,subQ82,subQ77,subQ128,subQ127,subQ126,subQ125,subQ124,subQ123,subQ73,subQ69,subQ65,subQ53,subQ49,subQ45,subQ41,subQ122,subQ28,subQ18,subQ121,subQ120,subQ119,subQ61,subQ33,subQ118,subQ117,subQ116,subQ115,subQ114,subQ113,subQ112,subQ111,subQ110,subQ109,subQ108,subQ107,subQ106,subQ105,subQ104,subQ103,subQ102,subQ101,subQ100,subQ99,subQ98,subQ97,subQ96,subQ95,subQ94,subQ40,subQ44,subQ48,subQ52,subQ56,subQ81,subQ76,subQ93,subQ92,subQ91,subQ90,subQ89,subQ88,subQ72,subQ68,subQ64,subQ60,subQ87,subQ86,subQ85,subQ17,subQ27,subQ32])],"isStart":false});var subQ148=makeQuery(id+"F14.opExtrude","CAP_FACE",FACE,{"disambiguationData":[OSD([subQ135,subQ125,sQuery(id+"F6.wireOp",EDGE,"E97"),subQ90])],"isStart":true});var subQ149=makeQuery(id+"F17.opExtrude","SWEPT_FACE",FACE,{"disambiguationData":[OSD([subQ21])]});var subQ150=makeQuery(id+"F14.opExtrude","CAP_FACE",FACE,{"disambiguationData":[OSD([subQ133,subQ123,sQuery(id+"F6.wireOp",EDGE,"E101"),subQ88])],"isStart":true});var subQ151=makeQuery(id+"F14.opExtrude","CAP_FACE",FACE,{"disambiguationData":[OSD([subQ132,subQ121,sQuery(id+"F6.wireOp",EDGE,"E115"),subQ85])],"isStart":true});var subQ152=makeQuery(id+"F14.opExtrude","CAP_FACE",FACE,{"disambiguationData":[OSD([subQ131,subQ120,sQuery(id+"F6.wireOp",EDGE,"E113"),subQ86])],"isStart":true});var subQ153=makeQuery(id+"F14.opExtrude","CAP_FACE",FACE,{"disambiguationData":[OSD([subQ130,subQ119,sQuery(id+"F6.wireOp",EDGE,"E111"),subQ87])],"isStart":true});var subQ154=makeQuery(id+"F16.opRevolve","SWEPT_FACE",FACE,{"disambiguationData":[OSD([subQ36])]});var subQ155=makeQuery(id+"F17.opExtrude","SWEPT_FACE",FACE,{"disambiguationData":[OSD([subQ24])]});var subQ156=makeQuery(id+"F17.opExtrude","SWEPT_FACE",FACE,{"disambiguationData":[OSD([subQ22])]});Q7=makeQuery(id+"F27.opFillet","BLEND_EDGE",EDGE,{"blendedFrom":[makeQuery(id+"F19.boolean.opBoolean","INTERSECT",EDGE,{"derivedFrom":[makeQuery(id+"F18.boolean.opBoolean","SPLIT",FACE,{"disambiguationData":[TD([subQ31])],"derivedFrom":makeQuery(id+"F17.boolean.opBoolean","SPLIT",FACE,{"disambiguationData":[TD([makeQuery(id+"F13.opExtrude","SWEPT_FACE",FACE,{"disambiguationData":[OSD([subQ139])]}),subQ140,subQ147,subQ84,subQ79,subQ143,subQ144,subQ146,subQ148,subQ142,subQ150,subQ75,subQ71,subQ67,subQ63,subQ59,subQ55,subQ51,subQ47,subQ43,subQ35,subQ30,subQ20,subQ151,subQ152,subQ153,subQ141,subQ80,subQ39,subQ31,subQ154,subQ145,subQ26,subQ155,subQ16,subQ156,subQ149])],"derivedFrom":makeQuery(id+"F16.boolean.opBoolean","MERGE",FACE,{"derivedFrom":[subQ10,subQ9]})})}),subQ12]}),makeQuery(id+"F22.boolean.opBoolean","SPLIT",FACE,{"disambiguationData":[TD([subQ11])],"derivedFrom":makeQuery(id+"F21.boolean.opBoolean","MERGE",FACE,{"derivedFrom":[subQ16,subQ14,makeQuery(id+"F21.opExtrude","CAP_FACE",FACE,{"disambiguationData":[OSD([sQuery(id+"F11.wireOp",EDGE,"E292.MirrorCS"),sQuery(id+"F11.wireOp",EDGE,"E302"),sQuery(id+"F11.wireOp",EDGE,"E303"),subQ13,sQuery(id+"F11.wireOp",EDGE,"E305.0"),sQuery(id+"F11.wireOp",EDGE,"E305.1"),sQuery(id+"F11.wireOp",EDGE,"E305.2")])],"isStart":false})]})})],"blendedInto":[makeQuery(id+"F22.boolean.opBoolean","SPLIT",FACE,{"disambiguationData":[TD([subQ11])],"derivedFrom":makeQuery(id+"F21.boolean.opBoolean","MERGE",FACE,{"derivedFrom":[subQ16,subQ14,makeQuery(id+"F21.opExtrude","CAP_FACE",FACE,{"disambiguationData":[OSD([sQuery(id+"F11.wireOp",EDGE,"E292.MirrorCS"),sQuery(id+"F11.wireOp",EDGE,"E302"),sQuery(id+"F11.wireOp",EDGE,"E303"),subQ13,sQuery(id+"F11.wireOp",EDGE,"E305.0"),sQuery(id+"F11.wireOp",EDGE,"E305.1"),sQuery(id+"F11.wireOp",EDGE,"E305.2")])],"isStart":false})]})})]});}
            var Q8;
            {var subQ0=sQuery(id+"F10.wireOp",EDGE,"E285");var subQ1=sQuery(id+"F10.wireOp",EDGE,"E284");var subQ2=sQuery(id+"F10.wireOp",EDGE,"E283");var subQ3=sQuery(id+"F10.wireOp",EDGE,"E282");var subQ4=sQuery(id+"F10.wireOp",EDGE,"E281");var subQ5=sQuery(id+"F10.wireOp",EDGE,"E280");var subQ6=makeQuery(id+"F17.opExtrude","CAP_FACE",FACE,{"disambiguationData":[OSD([subQ5,subQ4,subQ3,subQ2,subQ1,subQ0])],"isStart":false});var subQ7=sQuery(id+"F7.wireOp",EDGE,"E150");var subQ8=makeQuery(id+"F16.opRevolve","SWEPT_FACE",FACE,{"disambiguationData":[OSD([subQ7])]});var subQ9=makeQuery(id+"F17.opExtrude","SWEPT_FACE",FACE,{"disambiguationData":[OSD([subQ4])]});var subQ10=sQuery(id+"F11.wireOp",EDGE,"E302");var subQ11=makeQuery(id+"F17.opExtrude","CAP_FACE",FACE,{"disambiguationData":[OSD([subQ5,subQ4,subQ3,subQ2,subQ1,subQ0])],"isStart":true});var subQ12=makeQuery(id+"F15.opRevolve","SWEPT_FACE",FACE,{"disambiguationData":[OSD([subQ7])]});var subQ13=makeQuery(id+"F19.opExtrude","SWEPT_FACE",FACE,{"disambiguationData":[OSD([sQuery(id+"F11.wireOp",EDGE,"E290.MirrorCS")])]});var subQ14=sQuery(id+"F9.wireOp",EDGE,"E256");var subQ15=makeQuery(id+"F18.opExtrude","SWEPT_FACE",FACE,{"disambiguationData":[OSD([subQ14])]});var subQ16=makeQuery(id+"F17.opExtrude","SWEPT_FACE",FACE,{"disambiguationData":[OSD([subQ3])]});var subQ17=sQuery(id+"F6.wireOp",EDGE,"E145");var subQ18=sQuery(id+"F6.wireOp",EDGE,"E69.MirrorCS");var subQ19=sQuery(id+"F6.wireOp",EDGE,"E46.MirrorCS");var subQ20=makeQuery(id+"F14.opExtrude","CAP_FACE",FACE,{"disambiguationData":[OSD([subQ19,subQ18,sQuery(id+"F6.wireOp",EDGE,"E117"),subQ17])],"isStart":true});var subQ21=sQuery(id+"F6.wireOp",EDGE,"E146");var subQ22=sQuery(id+"F6.wireOp",EDGE,"E68.MirrorCS");var subQ23=sQuery(id+"F6.wireOp",EDGE,"E45.MirrorCS");var subQ24=makeQuery(id+"F14.opExtrude","CAP_FACE",FACE,{"disambiguationData":[OSD([subQ23,subQ22,sQuery(id+"F6.wireOp",EDGE,"E120"),subQ21])],"isStart":true});var subQ25=makeQuery(id+"F16.opRevolve","SWEPT_FACE",FACE,{"disambiguationData":[OSD([sQuery(id+"F7.wireOp",EDGE,"E157")])]});var subQ26=sQuery(id+"F6.wireOp",EDGE,"E147");var subQ27=sQuery(id+"F6.wireOp",EDGE,"E74");var subQ28=sQuery(id+"F6.wireOp",EDGE,"E44.MirrorCS");var subQ29=makeQuery(id+"F14.opExtrude","CAP_FACE",FACE,{"disambiguationData":[OSD([subQ28,subQ27,sQuery(id+"F6.wireOp",EDGE,"E121"),subQ26])],"isStart":true});var subQ30=sQuery(id+"F7.wireOp",EDGE,"E164");var subQ31=sQuery(id+"F7.wireOp",EDGE,"E152");var subQ32=sQuery(id+"F7.wireOp",EDGE,"E151");var subQ33=makeQuery(id+"F15.opRevolve","CAP_FACE",FACE,{"disambiguationData":[OSD([subQ7,subQ32,subQ31,subQ30])],"isStart":false});var subQ34=sQuery(id+"F6.wireOp",EDGE,"E125");var subQ35=sQuery(id+"F6.wireOp",EDGE,"E66.MirrorCS");var subQ36=sQuery(id+"F6.wireOp",EDGE,"E43.MirrorCS");var subQ37=makeQuery(id+"F14.opExtrude","CAP_FACE",FACE,{"disambiguationData":[OSD([subQ36,subQ35,sQuery(id+"F6.wireOp",EDGE,"E77"),subQ34])],"isStart":true});var subQ38=sQuery(id+"F6.wireOp",EDGE,"E126");var subQ39=sQuery(id+"F6.wireOp",EDGE,"E65.MirrorCS");var subQ40=sQuery(id+"F6.wireOp",EDGE,"E42.MirrorCS");var subQ41=makeQuery(id+"F14.opExtrude","CAP_FACE",FACE,{"disambiguationData":[OSD([subQ40,subQ39,sQuery(id+"F6.wireOp",EDGE,"E79"),subQ38])],"isStart":true});var subQ42=sQuery(id+"F6.wireOp",EDGE,"E127");var subQ43=sQuery(id+"F6.wireOp",EDGE,"E64.MirrorCS");var subQ44=sQuery(id+"F6.wireOp",EDGE,"E41.MirrorCS");var subQ45=makeQuery(id+"F14.opExtrude","CAP_FACE",FACE,{"disambiguationData":[OSD([subQ44,subQ43,sQuery(id+"F6.wireOp",EDGE,"E81"),subQ42])],"isStart":true});var subQ46=sQuery(id+"F6.wireOp",EDGE,"E128");var subQ47=sQuery(id+"F6.wireOp",EDGE,"E63.MirrorCS");var subQ48=sQuery(id+"F6.wireOp",EDGE,"E40.MirrorCS");var subQ49=makeQuery(id+"F14.opExtrude","CAP_FACE",FACE,{"disambiguationData":[OSD([subQ48,subQ47,sQuery(id+"F6.wireOp",EDGE,"E83"),subQ46])],"isStart":true});var subQ50=sQuery(id+"F6.wireOp",EDGE,"E129");var subQ51=sQuery(id+"F6.wireOp",EDGE,"E51");var subQ52=sQuery(id+"F6.wireOp",EDGE,"E39.MirrorCS");var subQ53=makeQuery(id+"F14.opExtrude","CAP_FACE",FACE,{"disambiguationData":[OSD([subQ52,subQ51,sQuery(id+"F6.wireOp",EDGE,"E85"),subQ50])],"isStart":true});var subQ54=sQuery(id+"F6.wireOp",EDGE,"E141");var subQ55=sQuery(id+"F6.wireOp",EDGE,"E73");var subQ56=sQuery(id+"F6.wireOp",EDGE,"E38.MirrorCS");var subQ57=makeQuery(id+"F14.opExtrude","CAP_FACE",FACE,{"disambiguationData":[OSD([subQ56,subQ55,sQuery(id+"F6.wireOp",EDGE,"E109"),subQ54])],"isStart":true});var subQ58=sQuery(id+"F6.wireOp",EDGE,"E140");var subQ59=sQuery(id+"F6.wireOp",EDGE,"E62.MirrorCS");var subQ60=sQuery(id+"F6.wireOp",EDGE,"E37.MirrorCS");var subQ61=makeQuery(id+"F14.opExtrude","CAP_FACE",FACE,{"disambiguationData":[OSD([subQ60,subQ59,sQuery(id+"F6.wireOp",EDGE,"E107"),subQ58])],"isStart":true});var subQ62=sQuery(id+"F6.wireOp",EDGE,"E139");var subQ63=sQuery(id+"F6.wireOp",EDGE,"E61.MirrorCS");var subQ64=sQuery(id+"F6.wireOp",EDGE,"E36.MirrorCS");var subQ65=makeQuery(id+"F14.opExtrude","CAP_FACE",FACE,{"disambiguationData":[OSD([subQ64,subQ63,sQuery(id+"F6.wireOp",EDGE,"E105"),subQ62])],"isStart":true});var subQ66=sQuery(id+"F6.wireOp",EDGE,"E138");var subQ67=sQuery(id+"F6.wireOp",EDGE,"E60.MirrorCS");var subQ68=sQuery(id+"F6.wireOp",EDGE,"E35.MirrorCS");var subQ69=makeQuery(id+"F14.opExtrude","CAP_FACE",FACE,{"disambiguationData":[OSD([subQ68,subQ67,sQuery(id+"F6.wireOp",EDGE,"E103"),subQ66])],"isStart":true});var subQ70=sQuery(id+"F6.wireOp",EDGE,"E131");var subQ71=sQuery(id+"F6.wireOp",EDGE,"E53");var subQ72=sQuery(id+"F6.wireOp",EDGE,"E28");var subQ73=makeQuery(id+"F14.opExtrude","CAP_FACE",FACE,{"disambiguationData":[OSD([subQ72,subQ71,sQuery(id+"F6.wireOp",EDGE,"E89"),subQ70])],"isStart":true});var subQ74=makeQuery(id+"F15.opRevolve","CAP_FACE",FACE,{"disambiguationData":[OSD([subQ7,subQ32,subQ31,subQ30])],"isStart":true});var subQ75=sQuery(id+"F6.wireOp",EDGE,"E130");var subQ76=sQuery(id+"F6.wireOp",EDGE,"E52");var subQ77=sQuery(id+"F6.wireOp",EDGE,"E27");var subQ78=makeQuery(id+"F14.opExtrude","CAP_FACE",FACE,{"disambiguationData":[OSD([subQ77,subQ76,sQuery(id+"F6.wireOp",EDGE,"E87"),subQ75])],"isStart":true});var subQ79=sQuery(id+"F6.wireOp",EDGE,"E144");var subQ80=sQuery(id+"F6.wireOp",EDGE,"E143");var subQ81=sQuery(id+"F6.wireOp",EDGE,"E142");var subQ82=sQuery(id+"F6.wireOp",EDGE,"E137");var subQ83=sQuery(id+"F6.wireOp",EDGE,"E136");var subQ84=sQuery(id+"F6.wireOp",EDGE,"E135");var subQ85=sQuery(id+"F6.wireOp",EDGE,"E134");var subQ86=sQuery(id+"F6.wireOp",EDGE,"E133");var subQ87=sQuery(id+"F6.wireOp",EDGE,"E132");var subQ88=sQuery(id+"F6.wireOp",EDGE,"E124");var subQ89=sQuery(id+"F6.wireOp",EDGE,"E122");var subQ90=sQuery(id+"F6.wireOp",EDGE,"E119");var subQ91=sQuery(id+"F6.wireOp",EDGE,"E118");var subQ92=sQuery(id+"F6.wireOp",EDGE,"E116");var subQ93=sQuery(id+"F6.wireOp",EDGE,"E114");var subQ94=sQuery(id+"F6.wireOp",EDGE,"E112");var subQ95=sQuery(id+"F6.wireOp",EDGE,"E110");var subQ96=sQuery(id+"F6.wireOp",EDGE,"E108");var subQ97=sQuery(id+"F6.wireOp",EDGE,"E106");var subQ98=sQuery(id+"F6.wireOp",EDGE,"E104");var subQ99=sQuery(id+"F6.wireOp",EDGE,"E102");var subQ100=sQuery(id+"F6.wireOp",EDGE,"E100");var subQ101=sQuery(id+"F6.wireOp",EDGE,"E98");var subQ102=sQuery(id+"F6.wireOp",EDGE,"E96");var subQ103=sQuery(id+"F6.wireOp",EDGE,"E94");var subQ104=sQuery(id+"F6.wireOp",EDGE,"E92");var subQ105=sQuery(id+"F6.wireOp",EDGE,"E90");var subQ106=sQuery(id+"F6.wireOp",EDGE,"E88");var subQ107=sQuery(id+"F6.wireOp",EDGE,"E86");var subQ108=sQuery(id+"F6.wireOp",EDGE,"E84");var subQ109=sQuery(id+"F6.wireOp",EDGE,"E82");var subQ110=sQuery(id+"F6.wireOp",EDGE,"E80");var subQ111=sQuery(id+"F6.wireOp",EDGE,"E78");var subQ112=sQuery(id+"F6.wireOp",EDGE,"E76");var subQ113=sQuery(id+"F6.wireOp",EDGE,"E72.MirrorCS");var subQ114=sQuery(id+"F6.wireOp",EDGE,"E71.MirrorCS");var subQ115=sQuery(id+"F6.wireOp",EDGE,"E70.MirrorCS");var subQ116=sQuery(id+"F6.wireOp",EDGE,"E67.MirrorCS");var subQ117=sQuery(id+"F6.wireOp",EDGE,"E59.MirrorCS");var subQ118=sQuery(id+"F6.wireOp",EDGE,"E58.MirrorCS");var subQ119=sQuery(id+"F6.wireOp",EDGE,"E57");var subQ120=sQuery(id+"F6.wireOp",EDGE,"E56");var subQ121=sQuery(id+"F6.wireOp",EDGE,"E55");var subQ122=sQuery(id+"F6.wireOp",EDGE,"E54");var subQ123=sQuery(id+"F6.wireOp",EDGE,"E50");var subQ124=sQuery(id+"F6.wireOp",EDGE,"E49");var subQ125=sQuery(id+"F6.wireOp",EDGE,"E48.MirrorCS");var subQ126=sQuery(id+"F6.wireOp",EDGE,"E47.MirrorCS");var subQ127=sQuery(id+"F6.wireOp",EDGE,"E34.MirrorCS");var subQ128=sQuery(id+"F6.wireOp",EDGE,"E33");var subQ129=sQuery(id+"F6.wireOp",EDGE,"E32");var subQ130=sQuery(id+"F6.wireOp",EDGE,"E31");var subQ131=sQuery(id+"F6.wireOp",EDGE,"E30");var subQ132=sQuery(id+"F6.wireOp",EDGE,"E29");var subQ133=sQuery(id+"F6.wireOp",EDGE,"E1.0");var subQ134=makeQuery(id+"F13.opExtrude","CAP_FACE",FACE,{"disambiguationData":[OSD([subQ133,subQ77,subQ72,subQ132,subQ131,subQ130,subQ129,subQ128,subQ127,subQ68,subQ64,subQ60,subQ56,subQ52,subQ48,subQ44,subQ40,subQ36,subQ28,subQ23,subQ19,subQ126,subQ125,subQ124,subQ123,subQ51,subQ76,subQ71,subQ122,subQ121,subQ120,subQ119,subQ118,subQ117,subQ67,subQ63,subQ59,subQ47,subQ43,subQ39,subQ35,subQ116,subQ22,subQ18,subQ115,subQ114,subQ113,subQ55,subQ27,subQ112,subQ111,subQ110,subQ109,subQ108,subQ107,subQ106,subQ105,subQ104,subQ103,subQ102,subQ101,subQ100,subQ99,subQ98,subQ97,subQ96,subQ95,subQ94,subQ93,subQ92,subQ91,subQ90,subQ89,subQ88,subQ34,subQ38,subQ42,subQ46,subQ50,subQ75,subQ70,subQ87,subQ86,subQ85,subQ84,subQ83,subQ82,subQ66,subQ62,subQ58,subQ54,subQ81,subQ80,subQ79,subQ17,subQ21,subQ26])],"isStart":true});var subQ135=makeQuery(id+"F14.opExtrude","CAP_FACE",FACE,{"disambiguationData":[OSD([subQ123,subQ116,sQuery(id+"F6.wireOp",EDGE,"E123"),subQ88])],"isStart":true});var subQ136=makeQuery(id+"F14.opExtrude","CAP_FACE",FACE,{"disambiguationData":[OSD([subQ128,subQ118,sQuery(id+"F6.wireOp",EDGE,"E99"),subQ83])],"isStart":true});var subQ138=makeQuery(id+"F14.opExtrude","CAP_FACE",FACE,{"disambiguationData":[OSD([subQ132,subQ122,sQuery(id+"F6.wireOp",EDGE,"E91"),subQ87])],"isStart":true});var subQ139=makeQuery(id+"F14.opExtrude","CAP_FACE",FACE,{"disambiguationData":[OSD([subQ131,subQ121,sQuery(id+"F6.wireOp",EDGE,"E93"),subQ86])],"isStart":true});var subQ140=makeQuery(id+"F14.opExtrude","CAP_FACE",FACE,{"disambiguationData":[OSD([subQ130,subQ120,sQuery(id+"F6.wireOp",EDGE,"E95"),subQ85])],"isStart":true});var subQ145=makeQuery(id+"F13.opExtrude","CAP_FACE",FACE,{"disambiguationData":[OSD([subQ133,subQ77,subQ72,subQ132,subQ131,subQ130,subQ129,subQ128,subQ127,subQ68,subQ64,subQ60,subQ56,subQ52,subQ48,subQ44,subQ40,subQ36,subQ28,subQ23,subQ19,subQ126,subQ125,subQ124,subQ123,subQ51,subQ76,subQ71,subQ122,subQ121,subQ120,subQ119,subQ118,subQ117,subQ67,subQ63,subQ59,subQ47,subQ43,subQ39,subQ35,subQ116,subQ22,subQ18,subQ115,subQ114,subQ113,subQ55,subQ27,subQ112,subQ111,subQ110,subQ109,subQ108,subQ107,subQ106,subQ105,subQ104,subQ103,subQ102,subQ101,subQ100,subQ99,subQ98,subQ97,subQ96,subQ95,subQ94,subQ93,subQ92,subQ91,subQ90,subQ89,subQ88,subQ34,subQ38,subQ42,subQ46,subQ50,subQ75,subQ70,subQ87,subQ86,subQ85,subQ84,subQ83,subQ82,subQ66,subQ62,subQ58,subQ54,subQ81,subQ80,subQ79,subQ17,subQ21,subQ26])],"isStart":false});var subQ146=makeQuery(id+"F14.opExtrude","CAP_FACE",FACE,{"disambiguationData":[OSD([subQ129,subQ119,sQuery(id+"F6.wireOp",EDGE,"E97"),subQ84])],"isStart":true});var subQ147=makeQuery(id+"F17.opExtrude","SWEPT_FACE",FACE,{"disambiguationData":[OSD([subQ0])]});var subQ148=makeQuery(id+"F14.opExtrude","CAP_FACE",FACE,{"disambiguationData":[OSD([subQ127,subQ117,sQuery(id+"F6.wireOp",EDGE,"E101"),subQ82])],"isStart":true});var subQ149=makeQuery(id+"F14.opExtrude","CAP_FACE",FACE,{"disambiguationData":[OSD([subQ126,subQ115,sQuery(id+"F6.wireOp",EDGE,"E115"),subQ79])],"isStart":true});var subQ150=makeQuery(id+"F14.opExtrude","CAP_FACE",FACE,{"disambiguationData":[OSD([subQ125,subQ114,sQuery(id+"F6.wireOp",EDGE,"E113"),subQ80])],"isStart":true});var subQ151=makeQuery(id+"F14.opExtrude","CAP_FACE",FACE,{"disambiguationData":[OSD([subQ124,subQ113,sQuery(id+"F6.wireOp",EDGE,"E111"),subQ81])],"isStart":true});var subQ152=makeQuery(id+"F16.opRevolve","SWEPT_FACE",FACE,{"disambiguationData":[OSD([subQ30])]});var subQ153=makeQuery(id+"F17.opExtrude","SWEPT_FACE",FACE,{"disambiguationData":[OSD([subQ1])]});Q8=makeQuery(id+"F27.opFillet","BLEND_EDGE",EDGE,{"blendedFrom":[makeQuery(id+"F19.boolean.opBoolean","INTERSECT",EDGE,{"derivedFrom":[makeQuery(id+"F18.boolean.opBoolean","SPLIT",FACE,{"disambiguationData":[TD([subQ25])],"derivedFrom":makeQuery(id+"F17.boolean.opBoolean","SPLIT",FACE,{"disambiguationData":[TD([makeQuery(id+"F13.opExtrude","SWEPT_FACE",FACE,{"disambiguationData":[OSD([subQ133])]}),subQ134,subQ145,subQ78,subQ73,subQ138,subQ139,subQ140,subQ146,subQ136,subQ148,subQ69,subQ65,subQ61,subQ57,subQ53,subQ49,subQ45,subQ41,subQ37,subQ29,subQ24,subQ20,subQ149,subQ150,subQ151,subQ135,subQ74,subQ33,subQ25,subQ152,subQ11,subQ6,subQ9,subQ16,subQ153,subQ147])],"derivedFrom":makeQuery(id+"F16.boolean.opBoolean","MERGE",FACE,{"derivedFrom":[subQ12,subQ8]})})}),subQ13]}),makeQuery(id+"F22.boolean.opBoolean","SPLIT",FACE,{"disambiguationData":[TD([subQ9])],"derivedFrom":makeQuery(id+"F21.boolean.opBoolean","MERGE",FACE,{"derivedFrom":[subQ16,subQ15,makeQuery(id+"F21.opExtrude","CAP_FACE",FACE,{"disambiguationData":[OSD([sQuery(id+"F11.wireOp",EDGE,"E292.MirrorCS"),subQ10,sQuery(id+"F11.wireOp",EDGE,"E303"),sQuery(id+"F11.wireOp",EDGE,"E304"),sQuery(id+"F11.wireOp",EDGE,"E305.0"),sQuery(id+"F11.wireOp",EDGE,"E305.1"),sQuery(id+"F11.wireOp",EDGE,"E305.2")])],"isStart":false})]})})],"blendedInto":[makeQuery(id+"F22.boolean.opBoolean","SPLIT",FACE,{"disambiguationData":[TD([subQ9])],"derivedFrom":makeQuery(id+"F21.boolean.opBoolean","MERGE",FACE,{"derivedFrom":[subQ16,subQ15,makeQuery(id+"F21.opExtrude","CAP_FACE",FACE,{"disambiguationData":[OSD([sQuery(id+"F11.wireOp",EDGE,"E292.MirrorCS"),subQ10,sQuery(id+"F11.wireOp",EDGE,"E303"),sQuery(id+"F11.wireOp",EDGE,"E304"),sQuery(id+"F11.wireOp",EDGE,"E305.0"),sQuery(id+"F11.wireOp",EDGE,"E305.1"),sQuery(id+"F11.wireOp",EDGE,"E305.2")])],"isStart":false})]})})]});}
            var Q9;
            Q9=makeQuery(id+"F23.opExtrude","CAP_EDGE",EDGE,{"disambiguationData":[OSD([sQuery(id+"F8.wireOp",EDGE,"E229")])],"isStart":true});
            var Q10;
            Q10=makeQuery(id+"F23.opExtrude","CAP_EDGE",EDGE,{"disambiguationData":[OSD([sQuery(id+"F8.wireOp",EDGE,"E230")])],"isStart":true});
            var Q11;
            Q11=makeQuery(id+"F23.opExtrude","CAP_EDGE",EDGE,{"disambiguationData":[OSD([sQuery(id+"F8.wireOp",EDGE,"E231")])],"isStart":true});
            fillet(context, id + "F28", {"entities" : qUnion([Q0, Q1, Q2, Q3, Q4, Q5, Q6, Q7, Q8, Q9, Q10, Q11]), "radius" : 2.6 * mm, "tangentPropagation" : true, "allowEdgeOverflow" : false});
        }
        {
            var Q0;
            Q0=qCreatedBy(id+"F5.planeOp",FACE);
            var sketch = newSketch(context, id + "F29", { "sketchPlane" : qUnion([Q0])});
            skCircle(sketch, "E325", {"center": v(0, 0) * mm, "radius": 1.5 * mm, "construction": true});
            skCircle(sketch, "E326", {"center": v(0, 55.8) * mm, "radius": 1.25 * mm, "construction": true});
            skLineSegment(sketch, "E327", {"start": v(0, 55.8) * mm, "end": v(0, 14) * mm, "construction": true});
            skSolve(sketch);
        }
        {
            var Q0;
            Q0=sQuery(id+"F29.wireOp",VERTEX,"E327.start");
            var Q1;
            Q1=makeQuery(id+"F13.opExtrude","SWEPT_BODY",BODY,{"disambiguationData":[OSD([sQuery(id+"F6.wireOp",EDGE,"E1.0"),sQuery(id+"F6.wireOp",EDGE,"E27"),sQuery(id+"F6.wireOp",EDGE,"E28"),sQuery(id+"F6.wireOp",EDGE,"E29"),sQuery(id+"F6.wireOp",EDGE,"E30"),sQuery(id+"F6.wireOp",EDGE,"E31"),sQuery(id+"F6.wireOp",EDGE,"E32"),sQuery(id+"F6.wireOp",EDGE,"E33"),sQuery(id+"F6.wireOp",EDGE,"E34.MirrorCS"),sQuery(id+"F6.wireOp",EDGE,"E35.MirrorCS"),sQuery(id+"F6.wireOp",EDGE,"E36.MirrorCS"),sQuery(id+"F6.wireOp",EDGE,"E37.MirrorCS"),sQuery(id+"F6.wireOp",EDGE,"E38.MirrorCS"),sQuery(id+"F6.wireOp",EDGE,"E39.MirrorCS"),sQuery(id+"F6.wireOp",EDGE,"E40.MirrorCS"),sQuery(id+"F6.wireOp",EDGE,"E41.MirrorCS"),sQuery(id+"F6.wireOp",EDGE,"E42.MirrorCS"),sQuery(id+"F6.wireOp",EDGE,"E43.MirrorCS"),sQuery(id+"F6.wireOp",EDGE,"E44.MirrorCS"),sQuery(id+"F6.wireOp",EDGE,"E45.MirrorCS"),sQuery(id+"F6.wireOp",EDGE,"E46.MirrorCS"),sQuery(id+"F6.wireOp",EDGE,"E47.MirrorCS"),sQuery(id+"F6.wireOp",EDGE,"E48.MirrorCS"),sQuery(id+"F6.wireOp",EDGE,"E49"),sQuery(id+"F6.wireOp",EDGE,"E50"),sQuery(id+"F6.wireOp",EDGE,"E51"),sQuery(id+"F6.wireOp",EDGE,"E52"),sQuery(id+"F6.wireOp",EDGE,"E53"),sQuery(id+"F6.wireOp",EDGE,"E54"),sQuery(id+"F6.wireOp",EDGE,"E55"),sQuery(id+"F6.wireOp",EDGE,"E56"),sQuery(id+"F6.wireOp",EDGE,"E57"),sQuery(id+"F6.wireOp",EDGE,"E58.MirrorCS"),sQuery(id+"F6.wireOp",EDGE,"E59.MirrorCS"),sQuery(id+"F6.wireOp",EDGE,"E60.MirrorCS"),sQuery(id+"F6.wireOp",EDGE,"E61.MirrorCS"),sQuery(id+"F6.wireOp",EDGE,"E62.MirrorCS"),sQuery(id+"F6.wireOp",EDGE,"E63.MirrorCS"),sQuery(id+"F6.wireOp",EDGE,"E64.MirrorCS"),sQuery(id+"F6.wireOp",EDGE,"E65.MirrorCS"),sQuery(id+"F6.wireOp",EDGE,"E66.MirrorCS"),sQuery(id+"F6.wireOp",EDGE,"E67.MirrorCS"),sQuery(id+"F6.wireOp",EDGE,"E68.MirrorCS"),sQuery(id+"F6.wireOp",EDGE,"E69.MirrorCS"),sQuery(id+"F6.wireOp",EDGE,"E70.MirrorCS"),sQuery(id+"F6.wireOp",EDGE,"E71.MirrorCS"),sQuery(id+"F6.wireOp",EDGE,"E72.MirrorCS"),sQuery(id+"F6.wireOp",EDGE,"E73"),sQuery(id+"F6.wireOp",EDGE,"E74"),sQuery(id+"F6.wireOp",EDGE,"E76"),sQuery(id+"F6.wireOp",EDGE,"E78"),sQuery(id+"F6.wireOp",EDGE,"E80"),sQuery(id+"F6.wireOp",EDGE,"E82"),sQuery(id+"F6.wireOp",EDGE,"E84"),sQuery(id+"F6.wireOp",EDGE,"E86"),sQuery(id+"F6.wireOp",EDGE,"E88"),sQuery(id+"F6.wireOp",EDGE,"E90"),sQuery(id+"F6.wireOp",EDGE,"E92"),sQuery(id+"F6.wireOp",EDGE,"E94"),sQuery(id+"F6.wireOp",EDGE,"E96"),sQuery(id+"F6.wireOp",EDGE,"E98"),sQuery(id+"F6.wireOp",EDGE,"E100"),sQuery(id+"F6.wireOp",EDGE,"E102"),sQuery(id+"F6.wireOp",EDGE,"E104"),sQuery(id+"F6.wireOp",EDGE,"E106"),sQuery(id+"F6.wireOp",EDGE,"E108"),sQuery(id+"F6.wireOp",EDGE,"E110"),sQuery(id+"F6.wireOp",EDGE,"E112"),sQuery(id+"F6.wireOp",EDGE,"E114"),sQuery(id+"F6.wireOp",EDGE,"E116"),sQuery(id+"F6.wireOp",EDGE,"E118"),sQuery(id+"F6.wireOp",EDGE,"E119"),sQuery(id+"F6.wireOp",EDGE,"E122"),sQuery(id+"F6.wireOp",EDGE,"E124"),sQuery(id+"F6.wireOp",EDGE,"E125"),sQuery(id+"F6.wireOp",EDGE,"E126"),sQuery(id+"F6.wireOp",EDGE,"E127"),sQuery(id+"F6.wireOp",EDGE,"E128"),sQuery(id+"F6.wireOp",EDGE,"E129"),sQuery(id+"F6.wireOp",EDGE,"E130"),sQuery(id+"F6.wireOp",EDGE,"E131"),sQuery(id+"F6.wireOp",EDGE,"E132"),sQuery(id+"F6.wireOp",EDGE,"E133"),sQuery(id+"F6.wireOp",EDGE,"E134"),sQuery(id+"F6.wireOp",EDGE,"E135"),sQuery(id+"F6.wireOp",EDGE,"E136"),sQuery(id+"F6.wireOp",EDGE,"E137"),sQuery(id+"F6.wireOp",EDGE,"E138"),sQuery(id+"F6.wireOp",EDGE,"E139"),sQuery(id+"F6.wireOp",EDGE,"E140"),sQuery(id+"F6.wireOp",EDGE,"E141"),sQuery(id+"F6.wireOp",EDGE,"E142"),sQuery(id+"F6.wireOp",EDGE,"E143"),sQuery(id+"F6.wireOp",EDGE,"E144"),sQuery(id+"F6.wireOp",EDGE,"E145"),sQuery(id+"F6.wireOp",EDGE,"E146"),sQuery(id+"F6.wireOp",EDGE,"E147")])]});
            hole(context, id + "F30", {"style" : HoleStyle.SIMPLE, "endStyle" : HoleEndStyle.BLIND, "oppositeDirection" : true, "holeDiameter" : 7 * mm, "holeDepth" : 4 * mm, "isTappedThrough" : true, "tappedDepth" : 12 * mm, "tapClearance" : 3, "startFromSketch" : true, "locations" : qUnion([Q0]), "scope" : qUnion([Q1])});
        }
    });
